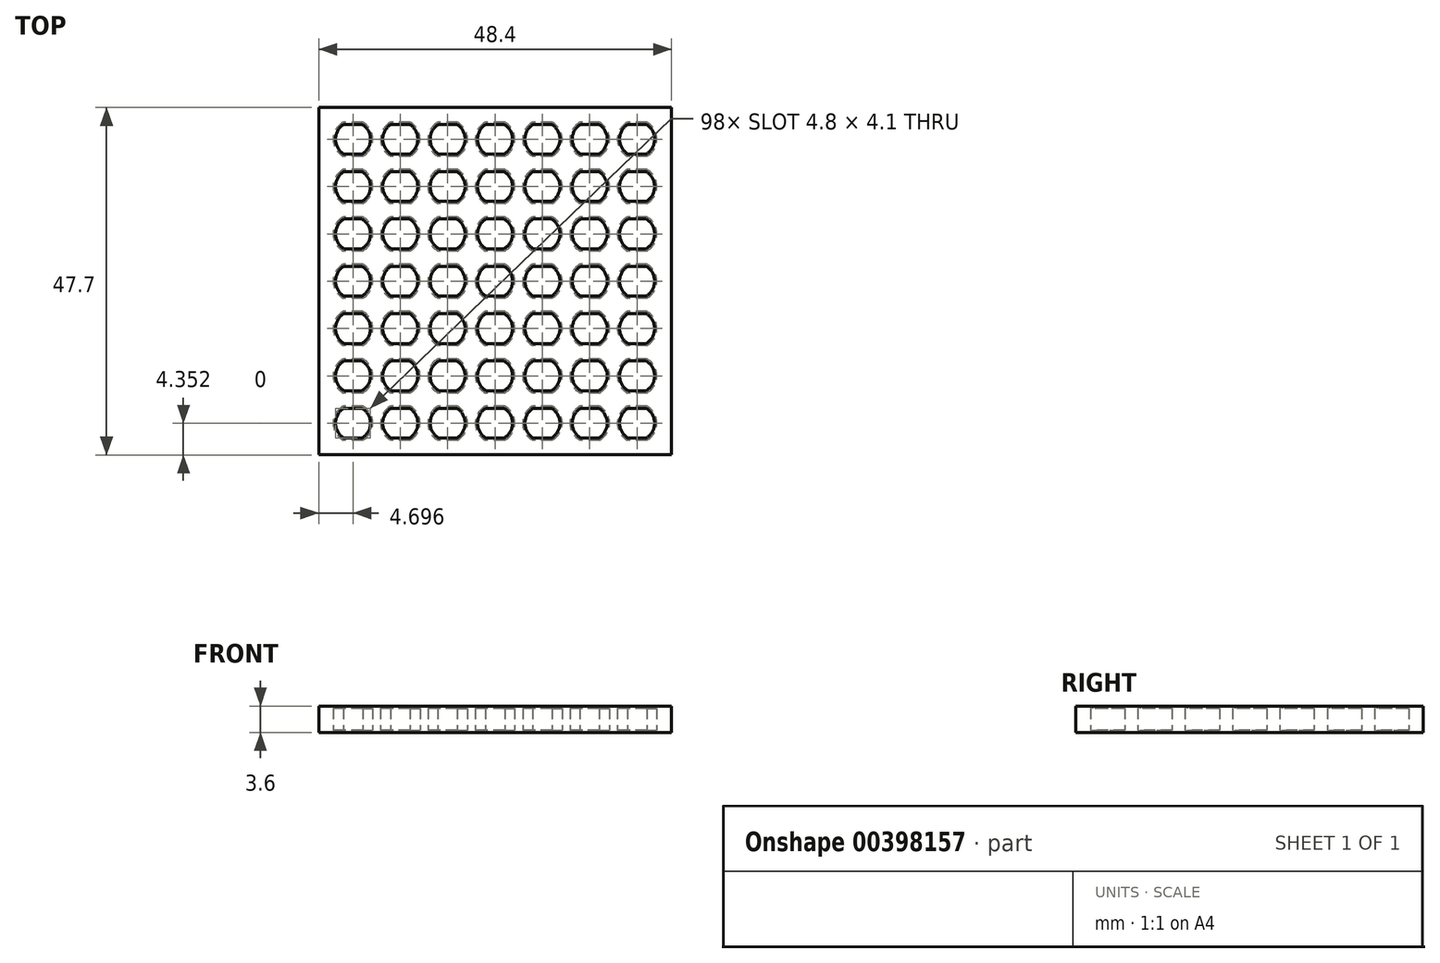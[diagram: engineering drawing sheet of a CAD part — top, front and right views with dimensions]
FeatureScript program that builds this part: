
annotation { "Feature Type Name" : "Feature", "Feature Type Description" : "" }
export const myFeature = defineFeature(function(context is Context, id is Id, definition is map)
    precondition{}
    {
        {
            var Q0;
            Q0=qCreatedBy(makeId("Top.planeOp"),FACE);
            var sketch = newSketch(context, id + "F0", { "sketchPlane" : qUnion([Q0])});
            skLineSegment(sketch, "E0.bottom", {"start": v(27.32, -19.22) * mm, "end": v(-27.32, -19.22) * mm, "construction": true});
            skLineSegment(sketch, "E0.top", {"start": v(27.32, 19.22) * mm, "end": v(-27.32, 19.22) * mm, "construction": true});
            skLineSegment(sketch, "E0.left", {"start": v(27.32, -19.22) * mm, "end": v(27.32, 19.22) * mm, "construction": true});
            skLineSegment(sketch, "E0.right", {"start": v(-27.32, -19.22) * mm, "end": v(-27.32, 19.22) * mm, "construction": true});
            skPoint(sketch, "E0.middle", {"position": v(0, 0) * mm});
            skArc(sketch, "E1", {"start": v(-23.3, 14.17) * mm, "mid": v(-21.92, 16.52) * mm, "end": v(-23.3, 18.87) * mm});
            skLineSegment(sketch, "E2.bottom", {"start": v(-23.3, 18.87) * mm, "end": v(-25.95, 18.87) * mm});
            skLineSegment(sketch, "E2.top", {"start": v(-23.3, 14.17) * mm, "end": v(-25.95, 14.17) * mm});
            skPoint(sketch, "E3.orphan", {"position": v(-21.92, 14.17) * mm});
            skPoint(sketch, "E4.orphan", {"position": v(-21.92, 18.87) * mm});
            skArc(sketch, "E5.trimOffspring", {"start": v(-25.95, 18.87) * mm, "mid": v(-27.32, 16.52) * mm, "end": v(-25.95, 14.17) * mm});
            skArc(sketch, "E6.0.1.0", {"start": v(-25.95, 12.37) * mm, "mid": v(-27.32, 10.02) * mm, "end": v(-25.95, 7.67) * mm});
            skLineSegment(sketch, "E6.0.1.1", {"start": v(-23.3, 7.67) * mm, "end": v(-25.95, 7.67) * mm});
            skLineSegment(sketch, "E6.0.1.2", {"start": v(-23.3, 12.37) * mm, "end": v(-25.95, 12.37) * mm});
            skArc(sketch, "E6.0.1.3", {"start": v(-23.3, 7.67) * mm, "mid": v(-21.92, 10.02) * mm, "end": v(-23.3, 12.37) * mm});
            skArc(sketch, "E6.0.2.0", {"start": v(-25.95, 5.87) * mm, "mid": v(-27.32, 3.52) * mm, "end": v(-25.95, 1.17) * mm});
            skLineSegment(sketch, "E6.0.2.1", {"start": v(-23.3, 1.17) * mm, "end": v(-25.95, 1.17) * mm});
            skLineSegment(sketch, "E6.0.2.2", {"start": v(-23.3, 5.87) * mm, "end": v(-25.95, 5.87) * mm});
            skArc(sketch, "E6.0.2.3", {"start": v(-23.3, 1.17) * mm, "mid": v(-21.92, 3.52) * mm, "end": v(-23.3, 5.87) * mm});
            skArc(sketch, "E6.1.0.0", {"start": v(-19.45, 18.87) * mm, "mid": v(-20.82, 16.52) * mm, "end": v(-19.45, 14.17) * mm});
            skLineSegment(sketch, "E6.1.0.1", {"start": v(-16.8, 14.17) * mm, "end": v(-19.45, 14.17) * mm});
            skLineSegment(sketch, "E6.1.0.2", {"start": v(-16.8, 18.87) * mm, "end": v(-19.45, 18.87) * mm});
            skArc(sketch, "E6.1.0.3", {"start": v(-16.8, 14.17) * mm, "mid": v(-15.42, 16.52) * mm, "end": v(-16.8, 18.87) * mm});
            skArc(sketch, "E6.1.1.0", {"start": v(-19.45, 12.37) * mm, "mid": v(-20.82, 10.02) * mm, "end": v(-19.45, 7.67) * mm});
            skLineSegment(sketch, "E6.1.1.1", {"start": v(-16.8, 7.67) * mm, "end": v(-19.45, 7.67) * mm});
            skLineSegment(sketch, "E6.1.1.2", {"start": v(-16.8, 12.37) * mm, "end": v(-19.45, 12.37) * mm});
            skArc(sketch, "E6.1.1.3", {"start": v(-16.8, 7.67) * mm, "mid": v(-15.42, 10.02) * mm, "end": v(-16.8, 12.37) * mm});
            skArc(sketch, "E6.1.2.0", {"start": v(-19.45, 5.87) * mm, "mid": v(-20.82, 3.52) * mm, "end": v(-19.45, 1.17) * mm});
            skLineSegment(sketch, "E6.1.2.1", {"start": v(-16.8, 1.17) * mm, "end": v(-19.45, 1.17) * mm});
            skLineSegment(sketch, "E6.1.2.2", {"start": v(-16.8, 5.87) * mm, "end": v(-19.45, 5.87) * mm});
            skArc(sketch, "E6.1.2.3", {"start": v(-16.8, 1.17) * mm, "mid": v(-15.42, 3.52) * mm, "end": v(-16.8, 5.87) * mm});
            skArc(sketch, "E6.2.0.0", {"start": v(-12.95, 18.87) * mm, "mid": v(-14.32, 16.52) * mm, "end": v(-12.95, 14.17) * mm});
            skLineSegment(sketch, "E6.2.0.1", {"start": v(-10.3, 14.17) * mm, "end": v(-12.95, 14.17) * mm});
            skLineSegment(sketch, "E6.2.0.2", {"start": v(-10.3, 18.87) * mm, "end": v(-12.95, 18.87) * mm});
            skArc(sketch, "E6.2.0.3", {"start": v(-10.3, 14.17) * mm, "mid": v(-8.92, 16.52) * mm, "end": v(-10.3, 18.87) * mm});
            skArc(sketch, "E6.2.1.0", {"start": v(-12.95, 12.37) * mm, "mid": v(-14.32, 10.02) * mm, "end": v(-12.95, 7.67) * mm});
            skLineSegment(sketch, "E6.2.1.1", {"start": v(-10.3, 7.67) * mm, "end": v(-12.95, 7.67) * mm});
            skLineSegment(sketch, "E6.2.1.2", {"start": v(-10.3, 12.37) * mm, "end": v(-12.95, 12.37) * mm});
            skArc(sketch, "E6.2.1.3", {"start": v(-10.3, 7.67) * mm, "mid": v(-8.92, 10.02) * mm, "end": v(-10.3, 12.37) * mm});
            skArc(sketch, "E6.2.2.0", {"start": v(-12.95, 5.87) * mm, "mid": v(-14.32, 3.52) * mm, "end": v(-12.95, 1.17) * mm});
            skLineSegment(sketch, "E6.2.2.1", {"start": v(-10.3, 1.17) * mm, "end": v(-12.95, 1.17) * mm});
            skLineSegment(sketch, "E6.2.2.2", {"start": v(-10.3, 5.87) * mm, "end": v(-12.95, 5.87) * mm});
            skArc(sketch, "E6.2.2.3", {"start": v(-10.3, 1.17) * mm, "mid": v(-8.92, 3.52) * mm, "end": v(-10.3, 5.87) * mm});
            skArc(sketch, "E6.3.0.0", {"start": v(-6.45, 18.87) * mm, "mid": v(-7.82, 16.52) * mm, "end": v(-6.45, 14.17) * mm});
            skLineSegment(sketch, "E6.3.0.1", {"start": v(-3.8, 14.17) * mm, "end": v(-6.45, 14.17) * mm});
            skLineSegment(sketch, "E6.3.0.2", {"start": v(-3.8, 18.87) * mm, "end": v(-6.45, 18.87) * mm});
            skArc(sketch, "E6.3.0.3", {"start": v(-3.8, 14.17) * mm, "mid": v(-2.42, 16.52) * mm, "end": v(-3.8, 18.87) * mm});
            skArc(sketch, "E6.3.1.0", {"start": v(-6.45, 12.37) * mm, "mid": v(-7.82, 10.02) * mm, "end": v(-6.45, 7.67) * mm});
            skLineSegment(sketch, "E6.3.1.1", {"start": v(-3.8, 7.67) * mm, "end": v(-6.45, 7.67) * mm});
            skLineSegment(sketch, "E6.3.1.2", {"start": v(-3.8, 12.37) * mm, "end": v(-6.45, 12.37) * mm});
            skArc(sketch, "E6.3.1.3", {"start": v(-3.8, 7.67) * mm, "mid": v(-2.42, 10.02) * mm, "end": v(-3.8, 12.37) * mm});
            skArc(sketch, "E6.3.2.0", {"start": v(-6.45, 5.87) * mm, "mid": v(-7.82, 3.52) * mm, "end": v(-6.45, 1.17) * mm});
            skLineSegment(sketch, "E6.3.2.1", {"start": v(-3.8, 1.17) * mm, "end": v(-6.45, 1.17) * mm});
            skLineSegment(sketch, "E6.3.2.2", {"start": v(-3.8, 5.87) * mm, "end": v(-6.45, 5.87) * mm});
            skArc(sketch, "E6.3.2.3", {"start": v(-3.8, 1.17) * mm, "mid": v(-2.42, 3.52) * mm, "end": v(-3.8, 5.87) * mm});
            skLineSegment(sketch, "E6.direction1", {"start": v(-25.95, 14.17) * mm, "end": v(-19.45, 14.17) * mm, "construction": true});
            skLineSegment(sketch, "E6.direction2", {"start": v(-25.95, 14.17) * mm, "end": v(-25.95, 7.67) * mm, "construction": true});
            skLineSegment(sketch, "E7.bottom", {"start": v(-29.32, 20.87) * mm, "end": v(19.08, 20.87) * mm});
            skLineSegment(sketch, "E7.top", {"start": v(-29.32, -26.83) * mm, "end": v(19.08, -26.83) * mm});
            skLineSegment(sketch, "E7.left", {"start": v(-29.32, 20.87) * mm, "end": v(-29.32, -26.83) * mm});
            skLineSegment(sketch, "E7.right", {"start": v(19.08, 20.87) * mm, "end": v(19.08, -26.83) * mm});
            skArc(sketch, "E8.0.4.0", {"start": v(0.05, 18.87) * mm, "mid": v(-1.32, 16.52) * mm, "end": v(0.05, 14.17) * mm});
            skLineSegment(sketch, "E8.4.4.0", {"start": v(2.7, 14.17) * mm, "end": v(0.05, 14.17) * mm});
            skLineSegment(sketch, "E8.7.4.0", {"start": v(2.7, 18.87) * mm, "end": v(0.05, 18.87) * mm});
            skArc(sketch, "E8.10.4.0", {"start": v(2.7, 14.17) * mm, "mid": v(4.08, 16.52) * mm, "end": v(2.7, 18.87) * mm});
            skArc(sketch, "E8.0.4.1", {"start": v(0.05, 12.37) * mm, "mid": v(-1.32, 10.02) * mm, "end": v(0.05, 7.67) * mm});
            skLineSegment(sketch, "E8.4.4.1", {"start": v(2.7, 7.67) * mm, "end": v(0.05, 7.67) * mm});
            skLineSegment(sketch, "E8.7.4.1", {"start": v(2.7, 12.37) * mm, "end": v(0.05, 12.37) * mm});
            skArc(sketch, "E8.10.4.1", {"start": v(2.7, 7.67) * mm, "mid": v(4.08, 10.02) * mm, "end": v(2.7, 12.37) * mm});
            skArc(sketch, "E8.0.4.2", {"start": v(0.05, 5.87) * mm, "mid": v(-1.32, 3.52) * mm, "end": v(0.05, 1.17) * mm});
            skLineSegment(sketch, "E8.4.4.2", {"start": v(2.7, 1.17) * mm, "end": v(0.05, 1.17) * mm});
            skLineSegment(sketch, "E8.7.4.2", {"start": v(2.7, 5.87) * mm, "end": v(0.05, 5.87) * mm});
            skArc(sketch, "E8.10.4.2", {"start": v(2.7, 1.17) * mm, "mid": v(4.08, 3.52) * mm, "end": v(2.7, 5.87) * mm});
            skArc(sketch, "E8.0.5.0", {"start": v(6.55, 18.87) * mm, "mid": v(5.18, 16.52) * mm, "end": v(6.55, 14.17) * mm});
            skLineSegment(sketch, "E8.4.5.0", {"start": v(9.2, 14.17) * mm, "end": v(6.55, 14.17) * mm});
            skLineSegment(sketch, "E8.7.5.0", {"start": v(9.2, 18.87) * mm, "end": v(6.55, 18.87) * mm});
            skArc(sketch, "E8.10.5.0", {"start": v(9.2, 14.17) * mm, "mid": v(10.58, 16.52) * mm, "end": v(9.2, 18.87) * mm});
            skArc(sketch, "E8.0.5.1", {"start": v(6.55, 12.37) * mm, "mid": v(5.18, 10.02) * mm, "end": v(6.55, 7.67) * mm});
            skLineSegment(sketch, "E8.4.5.1", {"start": v(9.2, 7.67) * mm, "end": v(6.55, 7.67) * mm});
            skLineSegment(sketch, "E8.7.5.1", {"start": v(9.2, 12.37) * mm, "end": v(6.55, 12.37) * mm});
            skArc(sketch, "E8.10.5.1", {"start": v(9.2, 7.67) * mm, "mid": v(10.58, 10.02) * mm, "end": v(9.2, 12.37) * mm});
            skArc(sketch, "E8.0.5.2", {"start": v(6.55, 5.87) * mm, "mid": v(5.18, 3.52) * mm, "end": v(6.55, 1.17) * mm});
            skLineSegment(sketch, "E8.4.5.2", {"start": v(9.2, 1.17) * mm, "end": v(6.55, 1.17) * mm});
            skLineSegment(sketch, "E8.7.5.2", {"start": v(9.2, 5.87) * mm, "end": v(6.55, 5.87) * mm});
            skArc(sketch, "E8.10.5.2", {"start": v(9.2, 1.17) * mm, "mid": v(10.58, 3.52) * mm, "end": v(9.2, 5.87) * mm});
            skArc(sketch, "E8.0.6.0", {"start": v(13.05, 18.87) * mm, "mid": v(11.68, 16.52) * mm, "end": v(13.05, 14.17) * mm});
            skLineSegment(sketch, "E8.4.6.0", {"start": v(15.7, 14.17) * mm, "end": v(13.05, 14.17) * mm});
            skLineSegment(sketch, "E8.7.6.0", {"start": v(15.7, 18.87) * mm, "end": v(13.05, 18.87) * mm});
            skArc(sketch, "E8.10.6.0", {"start": v(15.7, 14.17) * mm, "mid": v(17.08, 16.52) * mm, "end": v(15.7, 18.87) * mm});
            skArc(sketch, "E8.0.6.1", {"start": v(13.05, 12.37) * mm, "mid": v(11.68, 10.02) * mm, "end": v(13.05, 7.67) * mm});
            skLineSegment(sketch, "E8.4.6.1", {"start": v(15.7, 7.67) * mm, "end": v(13.05, 7.67) * mm});
            skLineSegment(sketch, "E8.7.6.1", {"start": v(15.7, 12.37) * mm, "end": v(13.05, 12.37) * mm});
            skArc(sketch, "E8.10.6.1", {"start": v(15.7, 7.67) * mm, "mid": v(17.08, 10.02) * mm, "end": v(15.7, 12.37) * mm});
            skArc(sketch, "E8.0.6.2", {"start": v(13.05, 5.87) * mm, "mid": v(11.68, 3.52) * mm, "end": v(13.05, 1.17) * mm});
            skLineSegment(sketch, "E8.4.6.2", {"start": v(15.7, 1.17) * mm, "end": v(13.05, 1.17) * mm});
            skLineSegment(sketch, "E8.7.6.2", {"start": v(15.7, 5.87) * mm, "end": v(13.05, 5.87) * mm});
            skArc(sketch, "E8.10.6.2", {"start": v(15.7, 1.17) * mm, "mid": v(17.08, 3.52) * mm, "end": v(15.7, 5.87) * mm});
            skArc(sketch, "E9.0.0.3", {"start": v(-25.95, -0.63) * mm, "mid": v(-27.32, -2.98) * mm, "end": v(-25.95, -5.33) * mm});
            skLineSegment(sketch, "E9.4.0.3", {"start": v(-23.3, -5.33) * mm, "end": v(-25.95, -5.33) * mm});
            skLineSegment(sketch, "E9.7.0.3", {"start": v(-23.3, -0.63) * mm, "end": v(-25.95, -0.63) * mm});
            skArc(sketch, "E9.10.0.3", {"start": v(-23.3, -5.33) * mm, "mid": v(-21.92, -2.98) * mm, "end": v(-23.3, -0.63) * mm});
            skArc(sketch, "E9.0.0.4", {"start": v(-25.95, -7.13) * mm, "mid": v(-27.32, -9.48) * mm, "end": v(-25.95, -11.83) * mm});
            skLineSegment(sketch, "E9.4.0.4", {"start": v(-23.3, -11.83) * mm, "end": v(-25.95, -11.83) * mm});
            skLineSegment(sketch, "E9.7.0.4", {"start": v(-23.3, -7.13) * mm, "end": v(-25.95, -7.13) * mm});
            skArc(sketch, "E9.10.0.4", {"start": v(-23.3, -11.83) * mm, "mid": v(-21.92, -9.48) * mm, "end": v(-23.3, -7.13) * mm});
            skArc(sketch, "E9.0.0.5", {"start": v(-25.95, -13.63) * mm, "mid": v(-27.32, -15.98) * mm, "end": v(-25.95, -18.33) * mm});
            skLineSegment(sketch, "E9.4.0.5", {"start": v(-23.3, -18.33) * mm, "end": v(-25.95, -18.33) * mm});
            skLineSegment(sketch, "E9.7.0.5", {"start": v(-23.3, -13.63) * mm, "end": v(-25.95, -13.63) * mm});
            skArc(sketch, "E9.10.0.5", {"start": v(-23.3, -18.33) * mm, "mid": v(-21.92, -15.98) * mm, "end": v(-23.3, -13.63) * mm});
            skArc(sketch, "E9.0.0.6", {"start": v(-25.95, -20.13) * mm, "mid": v(-27.32, -22.48) * mm, "end": v(-25.95, -24.83) * mm});
            skLineSegment(sketch, "E9.4.0.6", {"start": v(-23.3, -24.83) * mm, "end": v(-25.95, -24.83) * mm});
            skLineSegment(sketch, "E9.7.0.6", {"start": v(-23.3, -20.13) * mm, "end": v(-25.95, -20.13) * mm});
            skArc(sketch, "E9.10.0.6", {"start": v(-23.3, -24.83) * mm, "mid": v(-21.92, -22.48) * mm, "end": v(-23.3, -20.13) * mm});
            skArc(sketch, "E9.0.1.3", {"start": v(-19.45, -0.63) * mm, "mid": v(-20.82, -2.98) * mm, "end": v(-19.45, -5.33) * mm});
            skLineSegment(sketch, "E9.4.1.3", {"start": v(-16.8, -5.33) * mm, "end": v(-19.45, -5.33) * mm});
            skLineSegment(sketch, "E9.7.1.3", {"start": v(-16.8, -0.63) * mm, "end": v(-19.45, -0.63) * mm});
            skArc(sketch, "E9.10.1.3", {"start": v(-16.8, -5.33) * mm, "mid": v(-15.42, -2.98) * mm, "end": v(-16.8, -0.63) * mm});
            skArc(sketch, "E9.0.1.4", {"start": v(-19.45, -7.13) * mm, "mid": v(-20.82, -9.48) * mm, "end": v(-19.45, -11.83) * mm});
            skLineSegment(sketch, "E9.4.1.4", {"start": v(-16.8, -11.83) * mm, "end": v(-19.45, -11.83) * mm});
            skLineSegment(sketch, "E9.7.1.4", {"start": v(-16.8, -7.13) * mm, "end": v(-19.45, -7.13) * mm});
            skArc(sketch, "E9.10.1.4", {"start": v(-16.8, -11.83) * mm, "mid": v(-15.42, -9.48) * mm, "end": v(-16.8, -7.13) * mm});
            skArc(sketch, "E9.0.1.5", {"start": v(-19.45, -13.63) * mm, "mid": v(-20.82, -15.98) * mm, "end": v(-19.45, -18.33) * mm});
            skLineSegment(sketch, "E9.4.1.5", {"start": v(-16.8, -18.33) * mm, "end": v(-19.45, -18.33) * mm});
            skLineSegment(sketch, "E9.7.1.5", {"start": v(-16.8, -13.63) * mm, "end": v(-19.45, -13.63) * mm});
            skArc(sketch, "E9.10.1.5", {"start": v(-16.8, -18.33) * mm, "mid": v(-15.42, -15.98) * mm, "end": v(-16.8, -13.63) * mm});
            skArc(sketch, "E9.0.1.6", {"start": v(-19.45, -20.13) * mm, "mid": v(-20.82, -22.48) * mm, "end": v(-19.45, -24.83) * mm});
            skLineSegment(sketch, "E9.4.1.6", {"start": v(-16.8, -24.83) * mm, "end": v(-19.45, -24.83) * mm});
            skLineSegment(sketch, "E9.7.1.6", {"start": v(-16.8, -20.13) * mm, "end": v(-19.45, -20.13) * mm});
            skArc(sketch, "E9.10.1.6", {"start": v(-16.8, -24.83) * mm, "mid": v(-15.42, -22.48) * mm, "end": v(-16.8, -20.13) * mm});
            skArc(sketch, "E9.0.2.3", {"start": v(-12.95, -0.63) * mm, "mid": v(-14.32, -2.98) * mm, "end": v(-12.95, -5.33) * mm});
            skLineSegment(sketch, "E9.4.2.3", {"start": v(-10.3, -5.33) * mm, "end": v(-12.95, -5.33) * mm});
            skLineSegment(sketch, "E9.7.2.3", {"start": v(-10.3, -0.63) * mm, "end": v(-12.95, -0.63) * mm});
            skArc(sketch, "E9.10.2.3", {"start": v(-10.3, -5.33) * mm, "mid": v(-8.92, -2.98) * mm, "end": v(-10.3, -0.63) * mm});
            skArc(sketch, "E9.0.2.4", {"start": v(-12.95, -7.13) * mm, "mid": v(-14.32, -9.48) * mm, "end": v(-12.95, -11.83) * mm});
            skLineSegment(sketch, "E9.4.2.4", {"start": v(-10.3, -11.83) * mm, "end": v(-12.95, -11.83) * mm});
            skLineSegment(sketch, "E9.7.2.4", {"start": v(-10.3, -7.13) * mm, "end": v(-12.95, -7.13) * mm});
            skArc(sketch, "E9.10.2.4", {"start": v(-10.3, -11.83) * mm, "mid": v(-8.92, -9.48) * mm, "end": v(-10.3, -7.13) * mm});
            skArc(sketch, "E9.0.2.5", {"start": v(-12.95, -13.63) * mm, "mid": v(-14.32, -15.98) * mm, "end": v(-12.95, -18.33) * mm});
            skLineSegment(sketch, "E9.4.2.5", {"start": v(-10.3, -18.33) * mm, "end": v(-12.95, -18.33) * mm});
            skLineSegment(sketch, "E9.7.2.5", {"start": v(-10.3, -13.63) * mm, "end": v(-12.95, -13.63) * mm});
            skArc(sketch, "E9.10.2.5", {"start": v(-10.3, -18.33) * mm, "mid": v(-8.92, -15.98) * mm, "end": v(-10.3, -13.63) * mm});
            skArc(sketch, "E9.0.2.6", {"start": v(-12.95, -20.13) * mm, "mid": v(-14.32, -22.48) * mm, "end": v(-12.95, -24.83) * mm});
            skLineSegment(sketch, "E9.4.2.6", {"start": v(-10.3, -24.83) * mm, "end": v(-12.95, -24.83) * mm});
            skLineSegment(sketch, "E9.7.2.6", {"start": v(-10.3, -20.13) * mm, "end": v(-12.95, -20.13) * mm});
            skArc(sketch, "E9.10.2.6", {"start": v(-10.3, -24.83) * mm, "mid": v(-8.92, -22.48) * mm, "end": v(-10.3, -20.13) * mm});
            skArc(sketch, "E9.0.3.3", {"start": v(-6.45, -0.63) * mm, "mid": v(-7.82, -2.98) * mm, "end": v(-6.45, -5.33) * mm});
            skLineSegment(sketch, "E9.4.3.3", {"start": v(-3.8, -5.33) * mm, "end": v(-6.45, -5.33) * mm});
            skLineSegment(sketch, "E9.7.3.3", {"start": v(-3.8, -0.63) * mm, "end": v(-6.45, -0.63) * mm});
            skArc(sketch, "E9.10.3.3", {"start": v(-3.8, -5.33) * mm, "mid": v(-2.42, -2.98) * mm, "end": v(-3.8, -0.63) * mm});
            skArc(sketch, "E9.0.3.4", {"start": v(-6.45, -7.13) * mm, "mid": v(-7.82, -9.48) * mm, "end": v(-6.45, -11.83) * mm});
            skLineSegment(sketch, "E9.4.3.4", {"start": v(-3.8, -11.83) * mm, "end": v(-6.45, -11.83) * mm});
            skLineSegment(sketch, "E9.7.3.4", {"start": v(-3.8, -7.13) * mm, "end": v(-6.45, -7.13) * mm});
            skArc(sketch, "E9.10.3.4", {"start": v(-3.8, -11.83) * mm, "mid": v(-2.42, -9.48) * mm, "end": v(-3.8, -7.13) * mm});
            skArc(sketch, "E9.0.3.5", {"start": v(-6.45, -13.63) * mm, "mid": v(-7.82, -15.98) * mm, "end": v(-6.45, -18.33) * mm});
            skLineSegment(sketch, "E9.4.3.5", {"start": v(-3.8, -18.33) * mm, "end": v(-6.45, -18.33) * mm});
            skLineSegment(sketch, "E9.7.3.5", {"start": v(-3.8, -13.63) * mm, "end": v(-6.45, -13.63) * mm});
            skArc(sketch, "E9.10.3.5", {"start": v(-3.8, -18.33) * mm, "mid": v(-2.42, -15.98) * mm, "end": v(-3.8, -13.63) * mm});
            skArc(sketch, "E9.0.3.6", {"start": v(-6.45, -20.13) * mm, "mid": v(-7.82, -22.48) * mm, "end": v(-6.45, -24.83) * mm});
            skLineSegment(sketch, "E9.4.3.6", {"start": v(-3.8, -24.83) * mm, "end": v(-6.45, -24.83) * mm});
            skLineSegment(sketch, "E9.7.3.6", {"start": v(-3.8, -20.13) * mm, "end": v(-6.45, -20.13) * mm});
            skArc(sketch, "E9.10.3.6", {"start": v(-3.8, -24.83) * mm, "mid": v(-2.42, -22.48) * mm, "end": v(-3.8, -20.13) * mm});
            skArc(sketch, "E9.0.4.3", {"start": v(0.05, -0.63) * mm, "mid": v(-1.32, -2.98) * mm, "end": v(0.05, -5.33) * mm});
            skLineSegment(sketch, "E9.4.4.3", {"start": v(2.7, -5.33) * mm, "end": v(0.05, -5.33) * mm});
            skLineSegment(sketch, "E9.7.4.3", {"start": v(2.7, -0.63) * mm, "end": v(0.05, -0.63) * mm});
            skArc(sketch, "E9.10.4.3", {"start": v(2.7, -5.33) * mm, "mid": v(4.08, -2.98) * mm, "end": v(2.7, -0.63) * mm});
            skArc(sketch, "E9.0.4.4", {"start": v(0.05, -7.13) * mm, "mid": v(-1.32, -9.48) * mm, "end": v(0.05, -11.83) * mm});
            skLineSegment(sketch, "E9.4.4.4", {"start": v(2.7, -11.83) * mm, "end": v(0.05, -11.83) * mm});
            skLineSegment(sketch, "E9.7.4.4", {"start": v(2.7, -7.13) * mm, "end": v(0.05, -7.13) * mm});
            skArc(sketch, "E9.10.4.4", {"start": v(2.7, -11.83) * mm, "mid": v(4.08, -9.48) * mm, "end": v(2.7, -7.13) * mm});
            skArc(sketch, "E9.0.4.5", {"start": v(0.05, -13.63) * mm, "mid": v(-1.32, -15.98) * mm, "end": v(0.05, -18.33) * mm});
            skLineSegment(sketch, "E9.4.4.5", {"start": v(2.7, -18.33) * mm, "end": v(0.05, -18.33) * mm});
            skLineSegment(sketch, "E9.7.4.5", {"start": v(2.7, -13.63) * mm, "end": v(0.05, -13.63) * mm});
            skArc(sketch, "E9.10.4.5", {"start": v(2.7, -18.33) * mm, "mid": v(4.08, -15.98) * mm, "end": v(2.7, -13.63) * mm});
            skArc(sketch, "E9.0.4.6", {"start": v(0.05, -20.13) * mm, "mid": v(-1.32, -22.48) * mm, "end": v(0.05, -24.83) * mm});
            skLineSegment(sketch, "E9.4.4.6", {"start": v(2.7, -24.83) * mm, "end": v(0.05, -24.83) * mm});
            skLineSegment(sketch, "E9.7.4.6", {"start": v(2.7, -20.13) * mm, "end": v(0.05, -20.13) * mm});
            skArc(sketch, "E9.10.4.6", {"start": v(2.7, -24.83) * mm, "mid": v(4.08, -22.48) * mm, "end": v(2.7, -20.13) * mm});
            skArc(sketch, "E9.0.5.3", {"start": v(6.55, -0.63) * mm, "mid": v(5.18, -2.98) * mm, "end": v(6.55, -5.33) * mm});
            skLineSegment(sketch, "E9.4.5.3", {"start": v(9.2, -5.33) * mm, "end": v(6.55, -5.33) * mm});
            skLineSegment(sketch, "E9.7.5.3", {"start": v(9.2, -0.63) * mm, "end": v(6.55, -0.63) * mm});
            skArc(sketch, "E9.10.5.3", {"start": v(9.2, -5.33) * mm, "mid": v(10.58, -2.98) * mm, "end": v(9.2, -0.63) * mm});
            skArc(sketch, "E9.0.5.4", {"start": v(6.55, -7.13) * mm, "mid": v(5.18, -9.48) * mm, "end": v(6.55, -11.83) * mm});
            skLineSegment(sketch, "E9.4.5.4", {"start": v(9.2, -11.83) * mm, "end": v(6.55, -11.83) * mm});
            skLineSegment(sketch, "E9.7.5.4", {"start": v(9.2, -7.13) * mm, "end": v(6.55, -7.13) * mm});
            skArc(sketch, "E9.10.5.4", {"start": v(9.2, -11.83) * mm, "mid": v(10.58, -9.48) * mm, "end": v(9.2, -7.13) * mm});
            skArc(sketch, "E9.0.5.5", {"start": v(6.55, -13.63) * mm, "mid": v(5.18, -15.98) * mm, "end": v(6.55, -18.33) * mm});
            skLineSegment(sketch, "E9.4.5.5", {"start": v(9.2, -18.33) * mm, "end": v(6.55, -18.33) * mm});
            skLineSegment(sketch, "E9.7.5.5", {"start": v(9.2, -13.63) * mm, "end": v(6.55, -13.63) * mm});
            skArc(sketch, "E9.10.5.5", {"start": v(9.2, -18.33) * mm, "mid": v(10.58, -15.98) * mm, "end": v(9.2, -13.63) * mm});
            skArc(sketch, "E9.0.5.6", {"start": v(6.55, -20.13) * mm, "mid": v(5.18, -22.48) * mm, "end": v(6.55, -24.83) * mm});
            skLineSegment(sketch, "E9.4.5.6", {"start": v(9.2, -24.83) * mm, "end": v(6.55, -24.83) * mm});
            skLineSegment(sketch, "E9.7.5.6", {"start": v(9.2, -20.13) * mm, "end": v(6.55, -20.13) * mm});
            skArc(sketch, "E9.10.5.6", {"start": v(9.2, -24.83) * mm, "mid": v(10.58, -22.48) * mm, "end": v(9.2, -20.13) * mm});
            skArc(sketch, "E9.0.6.3", {"start": v(13.05, -0.63) * mm, "mid": v(11.68, -2.98) * mm, "end": v(13.05, -5.33) * mm});
            skLineSegment(sketch, "E9.4.6.3", {"start": v(15.7, -5.33) * mm, "end": v(13.05, -5.33) * mm});
            skLineSegment(sketch, "E9.7.6.3", {"start": v(15.7, -0.63) * mm, "end": v(13.05, -0.63) * mm});
            skArc(sketch, "E9.10.6.3", {"start": v(15.7, -5.33) * mm, "mid": v(17.08, -2.98) * mm, "end": v(15.7, -0.63) * mm});
            skArc(sketch, "E9.0.6.4", {"start": v(13.05, -7.13) * mm, "mid": v(11.68, -9.48) * mm, "end": v(13.05, -11.83) * mm});
            skLineSegment(sketch, "E9.4.6.4", {"start": v(15.7, -11.83) * mm, "end": v(13.05, -11.83) * mm});
            skLineSegment(sketch, "E9.7.6.4", {"start": v(15.7, -7.13) * mm, "end": v(13.05, -7.13) * mm});
            skArc(sketch, "E9.10.6.4", {"start": v(15.7, -11.83) * mm, "mid": v(17.08, -9.48) * mm, "end": v(15.7, -7.13) * mm});
            skArc(sketch, "E9.0.6.5", {"start": v(13.05, -13.63) * mm, "mid": v(11.68, -15.98) * mm, "end": v(13.05, -18.33) * mm});
            skLineSegment(sketch, "E9.4.6.5", {"start": v(15.7, -18.33) * mm, "end": v(13.05, -18.33) * mm});
            skLineSegment(sketch, "E9.7.6.5", {"start": v(15.7, -13.63) * mm, "end": v(13.05, -13.63) * mm});
            skArc(sketch, "E9.10.6.5", {"start": v(15.7, -18.33) * mm, "mid": v(17.08, -15.98) * mm, "end": v(15.7, -13.63) * mm});
            skArc(sketch, "E9.0.6.6", {"start": v(13.05, -20.13) * mm, "mid": v(11.68, -22.48) * mm, "end": v(13.05, -24.83) * mm});
            skLineSegment(sketch, "E9.4.6.6", {"start": v(15.7, -24.83) * mm, "end": v(13.05, -24.83) * mm});
            skLineSegment(sketch, "E9.7.6.6", {"start": v(15.7, -20.13) * mm, "end": v(13.05, -20.13) * mm});
            skArc(sketch, "E9.10.6.6", {"start": v(15.7, -24.83) * mm, "mid": v(17.08, -22.48) * mm, "end": v(15.7, -20.13) * mm});
            skLineSegment(sketch, "E10.bottom", {"start": v(-24.62, 16.52) * mm, "end": v(-18.12, 16.52) * mm, "construction": true});
            skLineSegment(sketch, "E10.top", {"start": v(-24.62, 10.02) * mm, "end": v(-18.12, 10.02) * mm, "construction": true});
            skLineSegment(sketch, "E10.left", {"start": v(-24.62, 16.52) * mm, "end": v(-24.62, 10.02) * mm, "construction": true});
            skLineSegment(sketch, "E10.right", {"start": v(-18.12, 16.52) * mm, "end": v(-18.12, 10.02) * mm, "construction": true});
            skSolve(sketch);
        }
        {
            var Q0;
            Q0=qSketchRegion(id+"F0",true);
            extrude(context, id + "F1", {"entities" : qUnion([Q0]), "depth" : 3 * mm});
        }
        {
            var Q0;
            Q0=makeQuery(id+"F1.opExtrude","CAP_FACE",FACE,{"disambiguationData":[OSD([sQuery(id+"F0.wireOp",EDGE,"E1"),sQuery(id+"F0.wireOp",EDGE,"E2.bottom"),sQuery(id+"F0.wireOp",EDGE,"E2.top"),sQuery(id+"F0.wireOp",EDGE,"E5.trimOffspring"),sQuery(id+"F0.wireOp",EDGE,"E6.0.1.0"),sQuery(id+"F0.wireOp",EDGE,"E6.0.1.1"),sQuery(id+"F0.wireOp",EDGE,"E6.0.1.2"),sQuery(id+"F0.wireOp",EDGE,"E6.0.1.3"),sQuery(id+"F0.wireOp",EDGE,"E6.0.2.0"),sQuery(id+"F0.wireOp",EDGE,"E6.0.2.1"),sQuery(id+"F0.wireOp",EDGE,"E6.0.2.2"),sQuery(id+"F0.wireOp",EDGE,"E6.0.2.3"),sQuery(id+"F0.wireOp",EDGE,"E6.1.0.0"),sQuery(id+"F0.wireOp",EDGE,"E6.1.0.1"),sQuery(id+"F0.wireOp",EDGE,"E6.1.0.2"),sQuery(id+"F0.wireOp",EDGE,"E6.1.0.3"),sQuery(id+"F0.wireOp",EDGE,"E6.1.1.0"),sQuery(id+"F0.wireOp",EDGE,"E6.1.1.1"),sQuery(id+"F0.wireOp",EDGE,"E6.1.1.2"),sQuery(id+"F0.wireOp",EDGE,"E6.1.1.3"),sQuery(id+"F0.wireOp",EDGE,"E6.1.2.0"),sQuery(id+"F0.wireOp",EDGE,"E6.1.2.1"),sQuery(id+"F0.wireOp",EDGE,"E6.1.2.2"),sQuery(id+"F0.wireOp",EDGE,"E6.1.2.3"),sQuery(id+"F0.wireOp",EDGE,"E6.2.0.0"),sQuery(id+"F0.wireOp",EDGE,"E6.2.0.1"),sQuery(id+"F0.wireOp",EDGE,"E6.2.0.2"),sQuery(id+"F0.wireOp",EDGE,"E6.2.0.3"),sQuery(id+"F0.wireOp",EDGE,"E6.2.1.0"),sQuery(id+"F0.wireOp",EDGE,"E6.2.1.1"),sQuery(id+"F0.wireOp",EDGE,"E6.2.1.2"),sQuery(id+"F0.wireOp",EDGE,"E6.2.1.3"),sQuery(id+"F0.wireOp",EDGE,"E6.2.2.0"),sQuery(id+"F0.wireOp",EDGE,"E6.2.2.1"),sQuery(id+"F0.wireOp",EDGE,"E6.2.2.2"),sQuery(id+"F0.wireOp",EDGE,"E6.2.2.3"),sQuery(id+"F0.wireOp",EDGE,"E6.3.0.0"),sQuery(id+"F0.wireOp",EDGE,"E6.3.0.1"),sQuery(id+"F0.wireOp",EDGE,"E6.3.0.2"),sQuery(id+"F0.wireOp",EDGE,"E6.3.0.3"),sQuery(id+"F0.wireOp",EDGE,"E6.3.1.0"),sQuery(id+"F0.wireOp",EDGE,"E6.3.1.1"),sQuery(id+"F0.wireOp",EDGE,"E6.3.1.2"),sQuery(id+"F0.wireOp",EDGE,"E6.3.1.3"),sQuery(id+"F0.wireOp",EDGE,"E6.3.2.0"),sQuery(id+"F0.wireOp",EDGE,"E6.3.2.1"),sQuery(id+"F0.wireOp",EDGE,"E6.3.2.2"),sQuery(id+"F0.wireOp",EDGE,"E6.3.2.3"),sQuery(id+"F0.wireOp",EDGE,"E7.bottom"),sQuery(id+"F0.wireOp",EDGE,"E7.top"),sQuery(id+"F0.wireOp",EDGE,"E7.left"),sQuery(id+"F0.wireOp",EDGE,"E7.right")])],"isStart":false});
            var sketch = newSketch(context, id + "F2", { "sketchPlane" : qUnion([Q0])});
            skLineSegment(sketch, "E11.0", {"start": v(-23.38, 18.57) * mm, "end": v(-25.87, 18.57) * mm});
            skArc(sketch, "E11.1", {"start": v(-23.38, 14.47) * mm, "mid": v(-22.22, 16.52) * mm, "end": v(-23.38, 18.57) * mm});
            skLineSegment(sketch, "E11.2", {"start": v(-23.38, 14.47) * mm, "end": v(-25.87, 14.47) * mm});
            skArc(sketch, "E11.3", {"start": v(-25.87, 18.57) * mm, "mid": v(-27.02, 16.52) * mm, "end": v(-25.87, 14.47) * mm});
            skArc(sketch, "E12.0.1.0", {"start": v(-25.87, 12.07) * mm, "mid": v(-27.02, 10.02) * mm, "end": v(-25.87, 7.97) * mm});
            skLineSegment(sketch, "E12.0.1.1", {"start": v(-23.38, 12.07) * mm, "end": v(-25.87, 12.07) * mm});
            skArc(sketch, "E12.0.1.2", {"start": v(-23.38, 7.97) * mm, "mid": v(-22.22, 10.02) * mm, "end": v(-23.38, 12.07) * mm});
            skLineSegment(sketch, "E12.0.1.3", {"start": v(-23.38, 7.97) * mm, "end": v(-25.87, 7.97) * mm});
            skArc(sketch, "E12.0.2.0", {"start": v(-25.87, 5.57) * mm, "mid": v(-27.02, 3.52) * mm, "end": v(-25.87, 1.47) * mm});
            skLineSegment(sketch, "E12.0.2.1", {"start": v(-23.38, 5.57) * mm, "end": v(-25.87, 5.57) * mm});
            skArc(sketch, "E12.0.2.2", {"start": v(-23.38, 1.47) * mm, "mid": v(-22.22, 3.52) * mm, "end": v(-23.38, 5.57) * mm});
            skLineSegment(sketch, "E12.0.2.3", {"start": v(-23.38, 1.47) * mm, "end": v(-25.87, 1.47) * mm});
            skArc(sketch, "E12.1.0.0", {"start": v(-19.37, 18.57) * mm, "mid": v(-20.52, 16.52) * mm, "end": v(-19.37, 14.47) * mm});
            skLineSegment(sketch, "E12.1.0.1", {"start": v(-16.88, 18.57) * mm, "end": v(-19.37, 18.57) * mm});
            skArc(sketch, "E12.1.0.2", {"start": v(-16.88, 14.47) * mm, "mid": v(-15.72, 16.52) * mm, "end": v(-16.88, 18.57) * mm});
            skLineSegment(sketch, "E12.1.0.3", {"start": v(-16.88, 14.47) * mm, "end": v(-19.37, 14.47) * mm});
            skArc(sketch, "E12.1.1.0", {"start": v(-19.37, 12.07) * mm, "mid": v(-20.52, 10.02) * mm, "end": v(-19.37, 7.97) * mm});
            skLineSegment(sketch, "E12.1.1.1", {"start": v(-16.88, 12.07) * mm, "end": v(-19.37, 12.07) * mm});
            skArc(sketch, "E12.1.1.2", {"start": v(-16.88, 7.97) * mm, "mid": v(-15.72, 10.02) * mm, "end": v(-16.88, 12.07) * mm});
            skLineSegment(sketch, "E12.1.1.3", {"start": v(-16.88, 7.97) * mm, "end": v(-19.37, 7.97) * mm});
            skArc(sketch, "E12.1.2.0", {"start": v(-19.37, 5.57) * mm, "mid": v(-20.52, 3.52) * mm, "end": v(-19.37, 1.47) * mm});
            skLineSegment(sketch, "E12.1.2.1", {"start": v(-16.88, 5.57) * mm, "end": v(-19.37, 5.57) * mm});
            skArc(sketch, "E12.1.2.2", {"start": v(-16.88, 1.47) * mm, "mid": v(-15.72, 3.52) * mm, "end": v(-16.88, 5.57) * mm});
            skLineSegment(sketch, "E12.1.2.3", {"start": v(-16.88, 1.47) * mm, "end": v(-19.37, 1.47) * mm});
            skArc(sketch, "E12.2.0.0", {"start": v(-12.87, 18.57) * mm, "mid": v(-14.02, 16.52) * mm, "end": v(-12.87, 14.47) * mm});
            skLineSegment(sketch, "E12.2.0.1", {"start": v(-10.38, 18.57) * mm, "end": v(-12.87, 18.57) * mm});
            skArc(sketch, "E12.2.0.2", {"start": v(-10.38, 14.47) * mm, "mid": v(-9.22, 16.52) * mm, "end": v(-10.38, 18.57) * mm});
            skLineSegment(sketch, "E12.2.0.3", {"start": v(-10.38, 14.47) * mm, "end": v(-12.87, 14.47) * mm});
            skArc(sketch, "E12.2.1.0", {"start": v(-12.87, 12.07) * mm, "mid": v(-14.02, 10.02) * mm, "end": v(-12.87, 7.97) * mm});
            skLineSegment(sketch, "E12.2.1.1", {"start": v(-10.38, 12.07) * mm, "end": v(-12.87, 12.07) * mm});
            skArc(sketch, "E12.2.1.2", {"start": v(-10.38, 7.97) * mm, "mid": v(-9.22, 10.02) * mm, "end": v(-10.38, 12.07) * mm});
            skLineSegment(sketch, "E12.2.1.3", {"start": v(-10.38, 7.97) * mm, "end": v(-12.87, 7.97) * mm});
            skArc(sketch, "E12.2.2.0", {"start": v(-12.87, 5.57) * mm, "mid": v(-14.02, 3.52) * mm, "end": v(-12.87, 1.47) * mm});
            skLineSegment(sketch, "E12.2.2.1", {"start": v(-10.38, 5.57) * mm, "end": v(-12.87, 5.57) * mm});
            skArc(sketch, "E12.2.2.2", {"start": v(-10.38, 1.47) * mm, "mid": v(-9.22, 3.52) * mm, "end": v(-10.38, 5.57) * mm});
            skLineSegment(sketch, "E12.2.2.3", {"start": v(-10.38, 1.47) * mm, "end": v(-12.87, 1.47) * mm});
            skArc(sketch, "E12.3.0.0", {"start": v(-6.37, 18.57) * mm, "mid": v(-7.52, 16.52) * mm, "end": v(-6.37, 14.47) * mm});
            skLineSegment(sketch, "E12.3.0.1", {"start": v(-3.88, 18.57) * mm, "end": v(-6.37, 18.57) * mm});
            skArc(sketch, "E12.3.0.2", {"start": v(-3.88, 14.47) * mm, "mid": v(-2.72, 16.52) * mm, "end": v(-3.88, 18.57) * mm});
            skLineSegment(sketch, "E12.3.0.3", {"start": v(-3.88, 14.47) * mm, "end": v(-6.37, 14.47) * mm});
            skArc(sketch, "E12.3.1.0", {"start": v(-6.37, 12.07) * mm, "mid": v(-7.52, 10.02) * mm, "end": v(-6.37, 7.97) * mm});
            skLineSegment(sketch, "E12.3.1.1", {"start": v(-3.88, 12.07) * mm, "end": v(-6.37, 12.07) * mm});
            skArc(sketch, "E12.3.1.2", {"start": v(-3.88, 7.97) * mm, "mid": v(-2.72, 10.02) * mm, "end": v(-3.88, 12.07) * mm});
            skLineSegment(sketch, "E12.3.1.3", {"start": v(-3.88, 7.97) * mm, "end": v(-6.37, 7.97) * mm});
            skArc(sketch, "E12.3.2.0", {"start": v(-6.37, 5.57) * mm, "mid": v(-7.52, 3.52) * mm, "end": v(-6.37, 1.47) * mm});
            skLineSegment(sketch, "E12.3.2.1", {"start": v(-3.88, 5.57) * mm, "end": v(-6.37, 5.57) * mm});
            skArc(sketch, "E12.3.2.2", {"start": v(-3.88, 1.47) * mm, "mid": v(-2.72, 3.52) * mm, "end": v(-3.88, 5.57) * mm});
            skLineSegment(sketch, "E12.3.2.3", {"start": v(-3.88, 1.47) * mm, "end": v(-6.37, 1.47) * mm});
            skLineSegment(sketch, "E12.direction1", {"start": v(-25.87, 14.47) * mm, "end": v(-19.37, 14.47) * mm, "construction": true});
            skLineSegment(sketch, "E12.direction2", {"start": v(-25.87, 14.47) * mm, "end": v(-25.87, 7.97) * mm, "construction": true});
            skLineSegment(sketch, "E13.bottom", {"start": v(-29.32, 20.87) * mm, "end": v(19.08, 20.87) * mm});
            skLineSegment(sketch, "E13.top", {"start": v(-29.32, -26.83) * mm, "end": v(19.08, -26.83) * mm});
            skLineSegment(sketch, "E13.left", {"start": v(-29.32, 20.87) * mm, "end": v(-29.32, -26.83) * mm});
            skLineSegment(sketch, "E13.right", {"start": v(19.08, 20.87) * mm, "end": v(19.08, -26.83) * mm});
            skArc(sketch, "E14.0.4.0", {"start": v(0.13, 18.57) * mm, "mid": v(-1.02, 16.52) * mm, "end": v(0.13, 14.47) * mm});
            skLineSegment(sketch, "E14.4.4.0", {"start": v(2.62, 18.57) * mm, "end": v(0.13, 18.57) * mm});
            skArc(sketch, "E14.7.4.0", {"start": v(2.62, 14.47) * mm, "mid": v(3.78, 16.52) * mm, "end": v(2.62, 18.57) * mm});
            skLineSegment(sketch, "E14.11.4.0", {"start": v(2.62, 14.47) * mm, "end": v(0.13, 14.47) * mm});
            skArc(sketch, "E14.0.4.1", {"start": v(0.13, 12.07) * mm, "mid": v(-1.02, 10.02) * mm, "end": v(0.13, 7.97) * mm});
            skLineSegment(sketch, "E14.4.4.1", {"start": v(2.62, 12.07) * mm, "end": v(0.13, 12.07) * mm});
            skArc(sketch, "E14.7.4.1", {"start": v(2.62, 7.97) * mm, "mid": v(3.78, 10.02) * mm, "end": v(2.62, 12.07) * mm});
            skLineSegment(sketch, "E14.11.4.1", {"start": v(2.62, 7.97) * mm, "end": v(0.13, 7.97) * mm});
            skArc(sketch, "E14.0.4.2", {"start": v(0.13, 5.57) * mm, "mid": v(-1.02, 3.52) * mm, "end": v(0.13, 1.47) * mm});
            skLineSegment(sketch, "E14.4.4.2", {"start": v(2.62, 5.57) * mm, "end": v(0.13, 5.57) * mm});
            skArc(sketch, "E14.7.4.2", {"start": v(2.62, 1.47) * mm, "mid": v(3.78, 3.52) * mm, "end": v(2.62, 5.57) * mm});
            skLineSegment(sketch, "E14.11.4.2", {"start": v(2.62, 1.47) * mm, "end": v(0.13, 1.47) * mm});
            skArc(sketch, "E14.0.5.0", {"start": v(6.63, 18.57) * mm, "mid": v(5.48, 16.52) * mm, "end": v(6.63, 14.47) * mm});
            skLineSegment(sketch, "E14.4.5.0", {"start": v(9.12, 18.57) * mm, "end": v(6.63, 18.57) * mm});
            skArc(sketch, "E14.7.5.0", {"start": v(9.12, 14.47) * mm, "mid": v(10.28, 16.52) * mm, "end": v(9.12, 18.57) * mm});
            skLineSegment(sketch, "E14.11.5.0", {"start": v(9.12, 14.47) * mm, "end": v(6.63, 14.47) * mm});
            skArc(sketch, "E14.0.5.1", {"start": v(6.63, 12.07) * mm, "mid": v(5.48, 10.02) * mm, "end": v(6.63, 7.97) * mm});
            skLineSegment(sketch, "E14.4.5.1", {"start": v(9.12, 12.07) * mm, "end": v(6.63, 12.07) * mm});
            skArc(sketch, "E14.7.5.1", {"start": v(9.12, 7.97) * mm, "mid": v(10.28, 10.02) * mm, "end": v(9.12, 12.07) * mm});
            skLineSegment(sketch, "E14.11.5.1", {"start": v(9.12, 7.97) * mm, "end": v(6.63, 7.97) * mm});
            skArc(sketch, "E14.0.5.2", {"start": v(6.63, 5.57) * mm, "mid": v(5.48, 3.52) * mm, "end": v(6.63, 1.47) * mm});
            skLineSegment(sketch, "E14.4.5.2", {"start": v(9.12, 5.57) * mm, "end": v(6.63, 5.57) * mm});
            skArc(sketch, "E14.7.5.2", {"start": v(9.12, 1.47) * mm, "mid": v(10.28, 3.52) * mm, "end": v(9.12, 5.57) * mm});
            skLineSegment(sketch, "E14.11.5.2", {"start": v(9.12, 1.47) * mm, "end": v(6.63, 1.47) * mm});
            skArc(sketch, "E14.0.6.0", {"start": v(13.13, 18.57) * mm, "mid": v(11.98, 16.52) * mm, "end": v(13.13, 14.47) * mm});
            skLineSegment(sketch, "E14.4.6.0", {"start": v(15.62, 18.57) * mm, "end": v(13.13, 18.57) * mm});
            skArc(sketch, "E14.7.6.0", {"start": v(15.62, 14.47) * mm, "mid": v(16.78, 16.52) * mm, "end": v(15.62, 18.57) * mm});
            skLineSegment(sketch, "E14.11.6.0", {"start": v(15.62, 14.47) * mm, "end": v(13.13, 14.47) * mm});
            skArc(sketch, "E14.0.6.1", {"start": v(13.13, 12.07) * mm, "mid": v(11.98, 10.02) * mm, "end": v(13.13, 7.97) * mm});
            skLineSegment(sketch, "E14.4.6.1", {"start": v(15.62, 12.07) * mm, "end": v(13.13, 12.07) * mm});
            skArc(sketch, "E14.7.6.1", {"start": v(15.62, 7.97) * mm, "mid": v(16.78, 10.02) * mm, "end": v(15.62, 12.07) * mm});
            skLineSegment(sketch, "E14.11.6.1", {"start": v(15.62, 7.97) * mm, "end": v(13.13, 7.97) * mm});
            skArc(sketch, "E14.0.6.2", {"start": v(13.13, 5.57) * mm, "mid": v(11.98, 3.52) * mm, "end": v(13.13, 1.47) * mm});
            skLineSegment(sketch, "E14.4.6.2", {"start": v(15.62, 5.57) * mm, "end": v(13.13, 5.57) * mm});
            skArc(sketch, "E14.7.6.2", {"start": v(15.62, 1.47) * mm, "mid": v(16.78, 3.52) * mm, "end": v(15.62, 5.57) * mm});
            skLineSegment(sketch, "E14.11.6.2", {"start": v(15.62, 1.47) * mm, "end": v(13.13, 1.47) * mm});
            skArc(sketch, "E15.0.0.3", {"start": v(-25.87, -0.93) * mm, "mid": v(-27.02, -2.98) * mm, "end": v(-25.87, -5.03) * mm});
            skLineSegment(sketch, "E15.4.0.3", {"start": v(-23.38, -0.93) * mm, "end": v(-25.87, -0.93) * mm});
            skArc(sketch, "E15.7.0.3", {"start": v(-23.38, -5.03) * mm, "mid": v(-22.22, -2.98) * mm, "end": v(-23.38, -0.93) * mm});
            skLineSegment(sketch, "E15.11.0.3", {"start": v(-23.38, -5.03) * mm, "end": v(-25.87, -5.03) * mm});
            skArc(sketch, "E15.0.0.4", {"start": v(-25.87, -7.43) * mm, "mid": v(-27.02, -9.48) * mm, "end": v(-25.87, -11.53) * mm});
            skLineSegment(sketch, "E15.4.0.4", {"start": v(-23.38, -7.43) * mm, "end": v(-25.87, -7.43) * mm});
            skArc(sketch, "E15.7.0.4", {"start": v(-23.38, -11.53) * mm, "mid": v(-22.22, -9.48) * mm, "end": v(-23.38, -7.43) * mm});
            skLineSegment(sketch, "E15.11.0.4", {"start": v(-23.38, -11.53) * mm, "end": v(-25.87, -11.53) * mm});
            skArc(sketch, "E15.0.0.5", {"start": v(-25.87, -13.93) * mm, "mid": v(-27.02, -15.98) * mm, "end": v(-25.87, -18.03) * mm});
            skLineSegment(sketch, "E15.4.0.5", {"start": v(-23.38, -13.93) * mm, "end": v(-25.87, -13.93) * mm});
            skArc(sketch, "E15.7.0.5", {"start": v(-23.38, -18.03) * mm, "mid": v(-22.22, -15.98) * mm, "end": v(-23.38, -13.93) * mm});
            skLineSegment(sketch, "E15.11.0.5", {"start": v(-23.38, -18.03) * mm, "end": v(-25.87, -18.03) * mm});
            skArc(sketch, "E15.0.0.6", {"start": v(-25.87, -20.43) * mm, "mid": v(-27.02, -22.48) * mm, "end": v(-25.87, -24.53) * mm});
            skLineSegment(sketch, "E15.4.0.6", {"start": v(-23.38, -20.43) * mm, "end": v(-25.87, -20.43) * mm});
            skArc(sketch, "E15.7.0.6", {"start": v(-23.38, -24.53) * mm, "mid": v(-22.22, -22.48) * mm, "end": v(-23.38, -20.43) * mm});
            skLineSegment(sketch, "E15.11.0.6", {"start": v(-23.38, -24.53) * mm, "end": v(-25.87, -24.53) * mm});
            skArc(sketch, "E15.0.1.3", {"start": v(-19.37, -0.93) * mm, "mid": v(-20.52, -2.98) * mm, "end": v(-19.37, -5.03) * mm});
            skLineSegment(sketch, "E15.4.1.3", {"start": v(-16.88, -0.93) * mm, "end": v(-19.37, -0.93) * mm});
            skArc(sketch, "E15.7.1.3", {"start": v(-16.88, -5.03) * mm, "mid": v(-15.72, -2.98) * mm, "end": v(-16.88, -0.93) * mm});
            skLineSegment(sketch, "E15.11.1.3", {"start": v(-16.88, -5.03) * mm, "end": v(-19.37, -5.03) * mm});
            skArc(sketch, "E15.0.1.4", {"start": v(-19.37, -7.43) * mm, "mid": v(-20.52, -9.48) * mm, "end": v(-19.37, -11.53) * mm});
            skLineSegment(sketch, "E15.4.1.4", {"start": v(-16.88, -7.43) * mm, "end": v(-19.37, -7.43) * mm});
            skArc(sketch, "E15.7.1.4", {"start": v(-16.88, -11.53) * mm, "mid": v(-15.72, -9.48) * mm, "end": v(-16.88, -7.43) * mm});
            skLineSegment(sketch, "E15.11.1.4", {"start": v(-16.88, -11.53) * mm, "end": v(-19.37, -11.53) * mm});
            skArc(sketch, "E15.0.1.5", {"start": v(-19.37, -13.93) * mm, "mid": v(-20.52, -15.98) * mm, "end": v(-19.37, -18.03) * mm});
            skLineSegment(sketch, "E15.4.1.5", {"start": v(-16.88, -13.93) * mm, "end": v(-19.37, -13.93) * mm});
            skArc(sketch, "E15.7.1.5", {"start": v(-16.88, -18.03) * mm, "mid": v(-15.72, -15.98) * mm, "end": v(-16.88, -13.93) * mm});
            skLineSegment(sketch, "E15.11.1.5", {"start": v(-16.88, -18.03) * mm, "end": v(-19.37, -18.03) * mm});
            skArc(sketch, "E15.0.1.6", {"start": v(-19.37, -20.43) * mm, "mid": v(-20.52, -22.48) * mm, "end": v(-19.37, -24.53) * mm});
            skLineSegment(sketch, "E15.4.1.6", {"start": v(-16.88, -20.43) * mm, "end": v(-19.37, -20.43) * mm});
            skArc(sketch, "E15.7.1.6", {"start": v(-16.88, -24.53) * mm, "mid": v(-15.72, -22.48) * mm, "end": v(-16.88, -20.43) * mm});
            skLineSegment(sketch, "E15.11.1.6", {"start": v(-16.88, -24.53) * mm, "end": v(-19.37, -24.53) * mm});
            skArc(sketch, "E15.0.2.3", {"start": v(-12.87, -0.93) * mm, "mid": v(-14.02, -2.98) * mm, "end": v(-12.87, -5.03) * mm});
            skLineSegment(sketch, "E15.4.2.3", {"start": v(-10.38, -0.93) * mm, "end": v(-12.87, -0.93) * mm});
            skArc(sketch, "E15.7.2.3", {"start": v(-10.38, -5.03) * mm, "mid": v(-9.22, -2.98) * mm, "end": v(-10.38, -0.93) * mm});
            skLineSegment(sketch, "E15.11.2.3", {"start": v(-10.38, -5.03) * mm, "end": v(-12.87, -5.03) * mm});
            skArc(sketch, "E15.0.2.4", {"start": v(-12.87, -7.43) * mm, "mid": v(-14.02, -9.48) * mm, "end": v(-12.87, -11.53) * mm});
            skLineSegment(sketch, "E15.4.2.4", {"start": v(-10.38, -7.43) * mm, "end": v(-12.87, -7.43) * mm});
            skArc(sketch, "E15.7.2.4", {"start": v(-10.38, -11.53) * mm, "mid": v(-9.22, -9.48) * mm, "end": v(-10.38, -7.43) * mm});
            skLineSegment(sketch, "E15.11.2.4", {"start": v(-10.38, -11.53) * mm, "end": v(-12.87, -11.53) * mm});
            skArc(sketch, "E15.0.2.5", {"start": v(-12.87, -13.93) * mm, "mid": v(-14.02, -15.98) * mm, "end": v(-12.87, -18.03) * mm});
            skLineSegment(sketch, "E15.4.2.5", {"start": v(-10.38, -13.93) * mm, "end": v(-12.87, -13.93) * mm});
            skArc(sketch, "E15.7.2.5", {"start": v(-10.38, -18.03) * mm, "mid": v(-9.22, -15.98) * mm, "end": v(-10.38, -13.93) * mm});
            skLineSegment(sketch, "E15.11.2.5", {"start": v(-10.38, -18.03) * mm, "end": v(-12.87, -18.03) * mm});
            skArc(sketch, "E15.0.2.6", {"start": v(-12.87, -20.43) * mm, "mid": v(-14.02, -22.48) * mm, "end": v(-12.87, -24.53) * mm});
            skLineSegment(sketch, "E15.4.2.6", {"start": v(-10.38, -20.43) * mm, "end": v(-12.87, -20.43) * mm});
            skArc(sketch, "E15.7.2.6", {"start": v(-10.38, -24.53) * mm, "mid": v(-9.22, -22.48) * mm, "end": v(-10.38, -20.43) * mm});
            skLineSegment(sketch, "E15.11.2.6", {"start": v(-10.38, -24.53) * mm, "end": v(-12.87, -24.53) * mm});
            skArc(sketch, "E15.0.3.3", {"start": v(-6.37, -0.93) * mm, "mid": v(-7.52, -2.98) * mm, "end": v(-6.37, -5.03) * mm});
            skLineSegment(sketch, "E15.4.3.3", {"start": v(-3.88, -0.93) * mm, "end": v(-6.37, -0.93) * mm});
            skArc(sketch, "E15.7.3.3", {"start": v(-3.88, -5.03) * mm, "mid": v(-2.72, -2.98) * mm, "end": v(-3.88, -0.93) * mm});
            skLineSegment(sketch, "E15.11.3.3", {"start": v(-3.88, -5.03) * mm, "end": v(-6.37, -5.03) * mm});
            skArc(sketch, "E15.0.3.4", {"start": v(-6.37, -7.43) * mm, "mid": v(-7.52, -9.48) * mm, "end": v(-6.37, -11.53) * mm});
            skLineSegment(sketch, "E15.4.3.4", {"start": v(-3.88, -7.43) * mm, "end": v(-6.37, -7.43) * mm});
            skArc(sketch, "E15.7.3.4", {"start": v(-3.88, -11.53) * mm, "mid": v(-2.72, -9.48) * mm, "end": v(-3.88, -7.43) * mm});
            skLineSegment(sketch, "E15.11.3.4", {"start": v(-3.88, -11.53) * mm, "end": v(-6.37, -11.53) * mm});
            skArc(sketch, "E15.0.3.5", {"start": v(-6.37, -13.93) * mm, "mid": v(-7.52, -15.98) * mm, "end": v(-6.37, -18.03) * mm});
            skLineSegment(sketch, "E15.4.3.5", {"start": v(-3.88, -13.93) * mm, "end": v(-6.37, -13.93) * mm});
            skArc(sketch, "E15.7.3.5", {"start": v(-3.88, -18.03) * mm, "mid": v(-2.72, -15.98) * mm, "end": v(-3.88, -13.93) * mm});
            skLineSegment(sketch, "E15.11.3.5", {"start": v(-3.88, -18.03) * mm, "end": v(-6.37, -18.03) * mm});
            skArc(sketch, "E15.0.3.6", {"start": v(-6.37, -20.43) * mm, "mid": v(-7.52, -22.48) * mm, "end": v(-6.37, -24.53) * mm});
            skLineSegment(sketch, "E15.4.3.6", {"start": v(-3.88, -20.43) * mm, "end": v(-6.37, -20.43) * mm});
            skArc(sketch, "E15.7.3.6", {"start": v(-3.88, -24.53) * mm, "mid": v(-2.72, -22.48) * mm, "end": v(-3.88, -20.43) * mm});
            skLineSegment(sketch, "E15.11.3.6", {"start": v(-3.88, -24.53) * mm, "end": v(-6.37, -24.53) * mm});
            skArc(sketch, "E15.0.4.3", {"start": v(0.13, -0.93) * mm, "mid": v(-1.02, -2.98) * mm, "end": v(0.13, -5.03) * mm});
            skLineSegment(sketch, "E15.4.4.3", {"start": v(2.62, -0.93) * mm, "end": v(0.13, -0.93) * mm});
            skArc(sketch, "E15.7.4.3", {"start": v(2.62, -5.03) * mm, "mid": v(3.78, -2.98) * mm, "end": v(2.62, -0.93) * mm});
            skLineSegment(sketch, "E15.11.4.3", {"start": v(2.62, -5.03) * mm, "end": v(0.13, -5.03) * mm});
            skArc(sketch, "E15.0.4.4", {"start": v(0.13, -7.43) * mm, "mid": v(-1.02, -9.48) * mm, "end": v(0.13, -11.53) * mm});
            skLineSegment(sketch, "E15.4.4.4", {"start": v(2.62, -7.43) * mm, "end": v(0.13, -7.43) * mm});
            skArc(sketch, "E15.7.4.4", {"start": v(2.62, -11.53) * mm, "mid": v(3.78, -9.48) * mm, "end": v(2.62, -7.43) * mm});
            skLineSegment(sketch, "E15.11.4.4", {"start": v(2.62, -11.53) * mm, "end": v(0.13, -11.53) * mm});
            skArc(sketch, "E15.0.4.5", {"start": v(0.13, -13.93) * mm, "mid": v(-1.02, -15.98) * mm, "end": v(0.13, -18.03) * mm});
            skLineSegment(sketch, "E15.4.4.5", {"start": v(2.62, -13.93) * mm, "end": v(0.13, -13.93) * mm});
            skArc(sketch, "E15.7.4.5", {"start": v(2.62, -18.03) * mm, "mid": v(3.78, -15.98) * mm, "end": v(2.62, -13.93) * mm});
            skLineSegment(sketch, "E15.11.4.5", {"start": v(2.62, -18.03) * mm, "end": v(0.13, -18.03) * mm});
            skArc(sketch, "E15.0.4.6", {"start": v(0.13, -20.43) * mm, "mid": v(-1.02, -22.48) * mm, "end": v(0.13, -24.53) * mm});
            skLineSegment(sketch, "E15.4.4.6", {"start": v(2.62, -20.43) * mm, "end": v(0.13, -20.43) * mm});
            skArc(sketch, "E15.7.4.6", {"start": v(2.62, -24.53) * mm, "mid": v(3.78, -22.48) * mm, "end": v(2.62, -20.43) * mm});
            skLineSegment(sketch, "E15.11.4.6", {"start": v(2.62, -24.53) * mm, "end": v(0.13, -24.53) * mm});
            skArc(sketch, "E15.0.5.3", {"start": v(6.63, -0.93) * mm, "mid": v(5.48, -2.98) * mm, "end": v(6.63, -5.03) * mm});
            skLineSegment(sketch, "E15.4.5.3", {"start": v(9.12, -0.93) * mm, "end": v(6.63, -0.93) * mm});
            skArc(sketch, "E15.7.5.3", {"start": v(9.12, -5.03) * mm, "mid": v(10.28, -2.98) * mm, "end": v(9.12, -0.93) * mm});
            skLineSegment(sketch, "E15.11.5.3", {"start": v(9.12, -5.03) * mm, "end": v(6.63, -5.03) * mm});
            skArc(sketch, "E15.0.5.4", {"start": v(6.63, -7.43) * mm, "mid": v(5.48, -9.48) * mm, "end": v(6.63, -11.53) * mm});
            skLineSegment(sketch, "E15.4.5.4", {"start": v(9.12, -7.43) * mm, "end": v(6.63, -7.43) * mm});
            skArc(sketch, "E15.7.5.4", {"start": v(9.12, -11.53) * mm, "mid": v(10.28, -9.48) * mm, "end": v(9.12, -7.43) * mm});
            skLineSegment(sketch, "E15.11.5.4", {"start": v(9.12, -11.53) * mm, "end": v(6.63, -11.53) * mm});
            skArc(sketch, "E15.0.5.5", {"start": v(6.63, -13.93) * mm, "mid": v(5.48, -15.98) * mm, "end": v(6.63, -18.03) * mm});
            skLineSegment(sketch, "E15.4.5.5", {"start": v(9.12, -13.93) * mm, "end": v(6.63, -13.93) * mm});
            skArc(sketch, "E15.7.5.5", {"start": v(9.12, -18.03) * mm, "mid": v(10.28, -15.98) * mm, "end": v(9.12, -13.93) * mm});
            skLineSegment(sketch, "E15.11.5.5", {"start": v(9.12, -18.03) * mm, "end": v(6.63, -18.03) * mm});
            skArc(sketch, "E15.0.5.6", {"start": v(6.63, -20.43) * mm, "mid": v(5.48, -22.48) * mm, "end": v(6.63, -24.53) * mm});
            skLineSegment(sketch, "E15.4.5.6", {"start": v(9.12, -20.43) * mm, "end": v(6.63, -20.43) * mm});
            skArc(sketch, "E15.7.5.6", {"start": v(9.12, -24.53) * mm, "mid": v(10.28, -22.48) * mm, "end": v(9.12, -20.43) * mm});
            skLineSegment(sketch, "E15.11.5.6", {"start": v(9.12, -24.53) * mm, "end": v(6.63, -24.53) * mm});
            skArc(sketch, "E15.0.6.3", {"start": v(13.13, -0.93) * mm, "mid": v(11.98, -2.98) * mm, "end": v(13.13, -5.03) * mm});
            skLineSegment(sketch, "E15.4.6.3", {"start": v(15.62, -0.93) * mm, "end": v(13.13, -0.93) * mm});
            skArc(sketch, "E15.7.6.3", {"start": v(15.62, -5.03) * mm, "mid": v(16.78, -2.98) * mm, "end": v(15.62, -0.93) * mm});
            skLineSegment(sketch, "E15.11.6.3", {"start": v(15.62, -5.03) * mm, "end": v(13.13, -5.03) * mm});
            skArc(sketch, "E15.0.6.4", {"start": v(13.13, -7.43) * mm, "mid": v(11.98, -9.48) * mm, "end": v(13.13, -11.53) * mm});
            skLineSegment(sketch, "E15.4.6.4", {"start": v(15.62, -7.43) * mm, "end": v(13.13, -7.43) * mm});
            skArc(sketch, "E15.7.6.4", {"start": v(15.62, -11.53) * mm, "mid": v(16.78, -9.48) * mm, "end": v(15.62, -7.43) * mm});
            skLineSegment(sketch, "E15.11.6.4", {"start": v(15.62, -11.53) * mm, "end": v(13.13, -11.53) * mm});
            skArc(sketch, "E15.0.6.5", {"start": v(13.13, -13.93) * mm, "mid": v(11.98, -15.98) * mm, "end": v(13.13, -18.03) * mm});
            skLineSegment(sketch, "E15.4.6.5", {"start": v(15.62, -13.93) * mm, "end": v(13.13, -13.93) * mm});
            skArc(sketch, "E15.7.6.5", {"start": v(15.62, -18.03) * mm, "mid": v(16.78, -15.98) * mm, "end": v(15.62, -13.93) * mm});
            skLineSegment(sketch, "E15.11.6.5", {"start": v(15.62, -18.03) * mm, "end": v(13.13, -18.03) * mm});
            skArc(sketch, "E15.0.6.6", {"start": v(13.13, -20.43) * mm, "mid": v(11.98, -22.48) * mm, "end": v(13.13, -24.53) * mm});
            skLineSegment(sketch, "E15.4.6.6", {"start": v(15.62, -20.43) * mm, "end": v(13.13, -20.43) * mm});
            skArc(sketch, "E15.7.6.6", {"start": v(15.62, -24.53) * mm, "mid": v(16.78, -22.48) * mm, "end": v(15.62, -20.43) * mm});
            skLineSegment(sketch, "E15.11.6.6", {"start": v(15.62, -24.53) * mm, "end": v(13.13, -24.53) * mm});
            skSolve(sketch);
        }
        {
            var Q0;
            Q0=qSketchRegion(id+"F2",true);
            extrude(context, id + "F3", {"entities" : qUnion([Q0]), "operationType" : NewBodyOperationType.ADD, "depth" : 0.3 * mm});
        }
        {
            var Q0;
            Q0=makeQuery(id+"F0.imprint","IMPRINT",FACE,{"disambiguationData":[TD([[makeQuery(id+"F0.imprint","IMPRINT",EDGE,{"derivedFrom":sQuery(id+"F0.wireOp",EDGE,"E1")}),-1.0]])]});
            var sketch = newSketch(context, id + "F4", { "sketchPlane" : qUnion([Q0])});
            skArc(sketch, "E16.0", {"start": v(-25.87, 5.57) * mm, "mid": v(-27.02, 3.52) * mm, "end": v(-25.87, 1.47) * mm});
            skLineSegment(sketch, "E16.1", {"start": v(-23.38, 5.57) * mm, "end": v(-25.87, 5.57) * mm});
            skArc(sketch, "E16.2", {"start": v(-23.38, 1.47) * mm, "mid": v(-22.22, 3.52) * mm, "end": v(-23.38, 5.57) * mm});
            skLineSegment(sketch, "E16.3", {"start": v(-23.38, 1.47) * mm, "end": v(-25.87, 1.47) * mm});
            skArc(sketch, "E17.0.1.0", {"start": v(-23.38, 7.97) * mm, "mid": v(-22.22, 10.02) * mm, "end": v(-23.38, 12.07) * mm});
            skLineSegment(sketch, "E17.0.1.1", {"start": v(-23.38, 7.97) * mm, "end": v(-25.87, 7.97) * mm});
            skArc(sketch, "E17.0.1.2", {"start": v(-25.87, 12.07) * mm, "mid": v(-27.02, 10.02) * mm, "end": v(-25.87, 7.97) * mm});
            skLineSegment(sketch, "E17.0.1.3", {"start": v(-23.38, 12.07) * mm, "end": v(-25.87, 12.07) * mm});
            skArc(sketch, "E17.0.2.0", {"start": v(-23.38, 14.47) * mm, "mid": v(-22.22, 16.52) * mm, "end": v(-23.38, 18.57) * mm});
            skLineSegment(sketch, "E17.0.2.1", {"start": v(-23.38, 14.47) * mm, "end": v(-25.87, 14.47) * mm});
            skArc(sketch, "E17.0.2.2", {"start": v(-25.87, 18.57) * mm, "mid": v(-27.02, 16.52) * mm, "end": v(-25.87, 14.47) * mm});
            skLineSegment(sketch, "E17.0.2.3", {"start": v(-23.38, 18.57) * mm, "end": v(-25.87, 18.57) * mm});
            skArc(sketch, "E17.1.0.0", {"start": v(-16.88, 1.47) * mm, "mid": v(-15.72, 3.52) * mm, "end": v(-16.88, 5.57) * mm});
            skLineSegment(sketch, "E17.1.0.1", {"start": v(-16.88, 1.47) * mm, "end": v(-19.37, 1.47) * mm});
            skArc(sketch, "E17.1.0.2", {"start": v(-19.37, 5.57) * mm, "mid": v(-20.52, 3.52) * mm, "end": v(-19.37, 1.47) * mm});
            skLineSegment(sketch, "E17.1.0.3", {"start": v(-16.88, 5.57) * mm, "end": v(-19.37, 5.57) * mm});
            skArc(sketch, "E17.1.1.0", {"start": v(-16.88, 7.97) * mm, "mid": v(-15.72, 10.02) * mm, "end": v(-16.88, 12.07) * mm});
            skLineSegment(sketch, "E17.1.1.1", {"start": v(-16.88, 7.97) * mm, "end": v(-19.37, 7.97) * mm});
            skArc(sketch, "E17.1.1.2", {"start": v(-19.37, 12.07) * mm, "mid": v(-20.52, 10.02) * mm, "end": v(-19.37, 7.97) * mm});
            skLineSegment(sketch, "E17.1.1.3", {"start": v(-16.88, 12.07) * mm, "end": v(-19.37, 12.07) * mm});
            skArc(sketch, "E17.1.2.0", {"start": v(-16.88, 14.47) * mm, "mid": v(-15.72, 16.52) * mm, "end": v(-16.88, 18.57) * mm});
            skLineSegment(sketch, "E17.1.2.1", {"start": v(-16.88, 14.47) * mm, "end": v(-19.37, 14.47) * mm});
            skArc(sketch, "E17.1.2.2", {"start": v(-19.37, 18.57) * mm, "mid": v(-20.52, 16.52) * mm, "end": v(-19.37, 14.47) * mm});
            skLineSegment(sketch, "E17.1.2.3", {"start": v(-16.88, 18.57) * mm, "end": v(-19.37, 18.57) * mm});
            skArc(sketch, "E17.2.0.0", {"start": v(-10.38, 1.47) * mm, "mid": v(-9.22, 3.52) * mm, "end": v(-10.38, 5.57) * mm});
            skLineSegment(sketch, "E17.2.0.1", {"start": v(-10.38, 1.47) * mm, "end": v(-12.87, 1.47) * mm});
            skArc(sketch, "E17.2.0.2", {"start": v(-12.87, 5.57) * mm, "mid": v(-14.02, 3.52) * mm, "end": v(-12.87, 1.47) * mm});
            skLineSegment(sketch, "E17.2.0.3", {"start": v(-10.38, 5.57) * mm, "end": v(-12.87, 5.57) * mm});
            skArc(sketch, "E17.2.1.0", {"start": v(-10.38, 7.97) * mm, "mid": v(-9.22, 10.02) * mm, "end": v(-10.38, 12.07) * mm});
            skLineSegment(sketch, "E17.2.1.1", {"start": v(-10.38, 7.97) * mm, "end": v(-12.87, 7.97) * mm});
            skArc(sketch, "E17.2.1.2", {"start": v(-12.87, 12.07) * mm, "mid": v(-14.02, 10.02) * mm, "end": v(-12.87, 7.97) * mm});
            skLineSegment(sketch, "E17.2.1.3", {"start": v(-10.38, 12.07) * mm, "end": v(-12.87, 12.07) * mm});
            skArc(sketch, "E17.2.2.0", {"start": v(-10.38, 14.47) * mm, "mid": v(-9.22, 16.52) * mm, "end": v(-10.38, 18.57) * mm});
            skLineSegment(sketch, "E17.2.2.1", {"start": v(-10.38, 14.47) * mm, "end": v(-12.87, 14.47) * mm});
            skArc(sketch, "E17.2.2.2", {"start": v(-12.87, 18.57) * mm, "mid": v(-14.02, 16.52) * mm, "end": v(-12.87, 14.47) * mm});
            skLineSegment(sketch, "E17.2.2.3", {"start": v(-10.38, 18.57) * mm, "end": v(-12.87, 18.57) * mm});
            skArc(sketch, "E17.3.0.0", {"start": v(-3.88, 1.47) * mm, "mid": v(-2.72, 3.52) * mm, "end": v(-3.88, 5.57) * mm});
            skLineSegment(sketch, "E17.3.0.1", {"start": v(-3.88, 1.47) * mm, "end": v(-6.37, 1.47) * mm});
            skArc(sketch, "E17.3.0.2", {"start": v(-6.37, 5.57) * mm, "mid": v(-7.52, 3.52) * mm, "end": v(-6.37, 1.47) * mm});
            skLineSegment(sketch, "E17.3.0.3", {"start": v(-3.88, 5.57) * mm, "end": v(-6.37, 5.57) * mm});
            skArc(sketch, "E17.3.1.0", {"start": v(-3.88, 7.97) * mm, "mid": v(-2.72, 10.02) * mm, "end": v(-3.88, 12.07) * mm});
            skLineSegment(sketch, "E17.3.1.1", {"start": v(-3.88, 7.97) * mm, "end": v(-6.37, 7.97) * mm});
            skArc(sketch, "E17.3.1.2", {"start": v(-6.37, 12.07) * mm, "mid": v(-7.52, 10.02) * mm, "end": v(-6.37, 7.97) * mm});
            skLineSegment(sketch, "E17.3.1.3", {"start": v(-3.88, 12.07) * mm, "end": v(-6.37, 12.07) * mm});
            skArc(sketch, "E17.3.2.0", {"start": v(-3.88, 14.47) * mm, "mid": v(-2.72, 16.52) * mm, "end": v(-3.88, 18.57) * mm});
            skLineSegment(sketch, "E17.3.2.1", {"start": v(-3.88, 14.47) * mm, "end": v(-6.37, 14.47) * mm});
            skArc(sketch, "E17.3.2.2", {"start": v(-6.37, 18.57) * mm, "mid": v(-7.52, 16.52) * mm, "end": v(-6.37, 14.47) * mm});
            skLineSegment(sketch, "E17.3.2.3", {"start": v(-3.88, 18.57) * mm, "end": v(-6.37, 18.57) * mm});
            skLineSegment(sketch, "E17.direction1", {"start": v(-25.87, 1.47) * mm, "end": v(-19.37, 1.47) * mm, "construction": true});
            skLineSegment(sketch, "E17.direction2", {"start": v(-25.87, 1.47) * mm, "end": v(-25.87, 7.97) * mm, "construction": true});
            skLineSegment(sketch, "E18.bottom", {"start": v(-29.32, -26.83) * mm, "end": v(19.08, -26.83) * mm});
            skLineSegment(sketch, "E18.top", {"start": v(-29.32, 20.87) * mm, "end": v(19.08, 20.87) * mm});
            skLineSegment(sketch, "E18.left", {"start": v(-29.32, -26.83) * mm, "end": v(-29.32, 20.87) * mm});
            skLineSegment(sketch, "E18.right", {"start": v(19.08, -26.83) * mm, "end": v(19.08, 20.87) * mm});
            skArc(sketch, "E19.0.4.0", {"start": v(2.62, 1.47) * mm, "mid": v(3.78, 3.52) * mm, "end": v(2.62, 5.57) * mm});
            skLineSegment(sketch, "E19.4.4.0", {"start": v(2.62, 1.47) * mm, "end": v(0.13, 1.47) * mm});
            skArc(sketch, "E19.7.4.0", {"start": v(0.13, 5.57) * mm, "mid": v(-1.02, 3.52) * mm, "end": v(0.13, 1.47) * mm});
            skLineSegment(sketch, "E19.11.4.0", {"start": v(2.62, 5.57) * mm, "end": v(0.13, 5.57) * mm});
            skArc(sketch, "E19.0.4.1", {"start": v(2.62, 7.97) * mm, "mid": v(3.78, 10.02) * mm, "end": v(2.62, 12.07) * mm});
            skLineSegment(sketch, "E19.4.4.1", {"start": v(2.62, 7.97) * mm, "end": v(0.13, 7.97) * mm});
            skArc(sketch, "E19.7.4.1", {"start": v(0.13, 12.07) * mm, "mid": v(-1.02, 10.02) * mm, "end": v(0.13, 7.97) * mm});
            skLineSegment(sketch, "E19.11.4.1", {"start": v(2.62, 12.07) * mm, "end": v(0.13, 12.07) * mm});
            skArc(sketch, "E19.0.4.2", {"start": v(2.62, 14.47) * mm, "mid": v(3.78, 16.52) * mm, "end": v(2.62, 18.57) * mm});
            skLineSegment(sketch, "E19.4.4.2", {"start": v(2.62, 14.47) * mm, "end": v(0.13, 14.47) * mm});
            skArc(sketch, "E19.7.4.2", {"start": v(0.13, 18.57) * mm, "mid": v(-1.02, 16.52) * mm, "end": v(0.13, 14.47) * mm});
            skLineSegment(sketch, "E19.11.4.2", {"start": v(2.62, 18.57) * mm, "end": v(0.13, 18.57) * mm});
            skArc(sketch, "E19.0.5.0", {"start": v(9.12, 1.47) * mm, "mid": v(10.28, 3.52) * mm, "end": v(9.12, 5.57) * mm});
            skLineSegment(sketch, "E19.4.5.0", {"start": v(9.12, 1.47) * mm, "end": v(6.63, 1.47) * mm});
            skArc(sketch, "E19.7.5.0", {"start": v(6.63, 5.57) * mm, "mid": v(5.48, 3.52) * mm, "end": v(6.63, 1.47) * mm});
            skLineSegment(sketch, "E19.11.5.0", {"start": v(9.12, 5.57) * mm, "end": v(6.63, 5.57) * mm});
            skArc(sketch, "E19.0.5.1", {"start": v(9.12, 7.97) * mm, "mid": v(10.28, 10.02) * mm, "end": v(9.12, 12.07) * mm});
            skLineSegment(sketch, "E19.4.5.1", {"start": v(9.12, 7.97) * mm, "end": v(6.63, 7.97) * mm});
            skArc(sketch, "E19.7.5.1", {"start": v(6.63, 12.07) * mm, "mid": v(5.48, 10.02) * mm, "end": v(6.63, 7.97) * mm});
            skLineSegment(sketch, "E19.11.5.1", {"start": v(9.12, 12.07) * mm, "end": v(6.63, 12.07) * mm});
            skArc(sketch, "E19.0.5.2", {"start": v(9.12, 14.47) * mm, "mid": v(10.28, 16.52) * mm, "end": v(9.12, 18.57) * mm});
            skLineSegment(sketch, "E19.4.5.2", {"start": v(9.12, 14.47) * mm, "end": v(6.63, 14.47) * mm});
            skArc(sketch, "E19.7.5.2", {"start": v(6.63, 18.57) * mm, "mid": v(5.48, 16.52) * mm, "end": v(6.63, 14.47) * mm});
            skLineSegment(sketch, "E19.11.5.2", {"start": v(9.12, 18.57) * mm, "end": v(6.63, 18.57) * mm});
            skArc(sketch, "E19.0.6.0", {"start": v(15.62, 1.47) * mm, "mid": v(16.78, 3.52) * mm, "end": v(15.62, 5.57) * mm});
            skLineSegment(sketch, "E19.4.6.0", {"start": v(15.62, 1.47) * mm, "end": v(13.13, 1.47) * mm});
            skArc(sketch, "E19.7.6.0", {"start": v(13.13, 5.57) * mm, "mid": v(11.98, 3.52) * mm, "end": v(13.13, 1.47) * mm});
            skLineSegment(sketch, "E19.11.6.0", {"start": v(15.62, 5.57) * mm, "end": v(13.13, 5.57) * mm});
            skArc(sketch, "E19.0.6.1", {"start": v(15.62, 7.97) * mm, "mid": v(16.78, 10.02) * mm, "end": v(15.62, 12.07) * mm});
            skLineSegment(sketch, "E19.4.6.1", {"start": v(15.62, 7.97) * mm, "end": v(13.13, 7.97) * mm});
            skArc(sketch, "E19.7.6.1", {"start": v(13.13, 12.07) * mm, "mid": v(11.98, 10.02) * mm, "end": v(13.13, 7.97) * mm});
            skLineSegment(sketch, "E19.11.6.1", {"start": v(15.62, 12.07) * mm, "end": v(13.13, 12.07) * mm});
            skArc(sketch, "E19.0.6.2", {"start": v(15.62, 14.47) * mm, "mid": v(16.78, 16.52) * mm, "end": v(15.62, 18.57) * mm});
            skLineSegment(sketch, "E19.4.6.2", {"start": v(15.62, 14.47) * mm, "end": v(13.13, 14.47) * mm});
            skArc(sketch, "E19.7.6.2", {"start": v(13.13, 18.57) * mm, "mid": v(11.98, 16.52) * mm, "end": v(13.13, 14.47) * mm});
            skLineSegment(sketch, "E19.11.6.2", {"start": v(15.62, 18.57) * mm, "end": v(13.13, 18.57) * mm});
            skArc(sketch, "E20.0.1.0", {"start": v(-12.87, -0.93) * mm, "mid": v(-14.02, -2.98) * mm, "end": v(-12.87, -5.03) * mm});
            skArc(sketch, "E20.0.1.1", {"start": v(-6.37, -0.93) * mm, "mid": v(-7.52, -2.98) * mm, "end": v(-6.37, -5.03) * mm});
            skLineSegment(sketch, "E20.0.1.2", {"start": v(2.62, -5.03) * mm, "end": v(0.13, -5.03) * mm});
            skLineSegment(sketch, "E20.0.1.3", {"start": v(15.62, -0.93) * mm, "end": v(13.13, -0.93) * mm});
            skArc(sketch, "E20.0.1.4", {"start": v(-19.37, -0.93) * mm, "mid": v(-20.52, -2.98) * mm, "end": v(-19.37, -5.03) * mm});
            skLineSegment(sketch, "E20.0.1.5", {"start": v(9.12, -5.03) * mm, "end": v(6.63, -5.03) * mm});
            skArc(sketch, "E20.0.1.6", {"start": v(15.62, -5.03) * mm, "mid": v(16.78, -2.98) * mm, "end": v(15.62, -0.93) * mm});
            skLineSegment(sketch, "E20.0.1.7", {"start": v(-16.88, -5.03) * mm, "end": v(-19.37, -5.03) * mm});
            skLineSegment(sketch, "E20.0.1.8", {"start": v(-10.38, -0.93) * mm, "end": v(-12.87, -0.93) * mm});
            skArc(sketch, "E20.0.1.9", {"start": v(0.13, -0.93) * mm, "mid": v(-1.02, -2.98) * mm, "end": v(0.13, -5.03) * mm});
            skLineSegment(sketch, "E20.0.1.10", {"start": v(15.62, -5.03) * mm, "end": v(13.13, -5.03) * mm});
            skArc(sketch, "E20.0.1.11", {"start": v(6.63, -0.93) * mm, "mid": v(5.48, -2.98) * mm, "end": v(6.63, -5.03) * mm});
            skLineSegment(sketch, "E20.0.1.12", {"start": v(-23.38, -0.93) * mm, "end": v(-25.87, -0.93) * mm});
            skArc(sketch, "E20.0.1.13", {"start": v(2.62, -5.03) * mm, "mid": v(3.78, -2.98) * mm, "end": v(2.62, -0.93) * mm});
            skArc(sketch, "E20.0.1.14", {"start": v(-10.38, -5.03) * mm, "mid": v(-9.22, -2.98) * mm, "end": v(-10.38, -0.93) * mm});
            skLineSegment(sketch, "E20.0.1.15", {"start": v(-23.38, -5.03) * mm, "end": v(-25.87, -5.03) * mm});
            skArc(sketch, "E20.0.1.16", {"start": v(-3.88, -5.03) * mm, "mid": v(-2.72, -2.98) * mm, "end": v(-3.88, -0.93) * mm});
            skLineSegment(sketch, "E20.0.1.17", {"start": v(-3.88, -0.93) * mm, "end": v(-6.37, -0.93) * mm});
            skLineSegment(sketch, "E20.0.1.18", {"start": v(2.62, -0.93) * mm, "end": v(0.13, -0.93) * mm});
            skLineSegment(sketch, "E20.0.1.19", {"start": v(-10.38, -5.03) * mm, "end": v(-12.87, -5.03) * mm});
            skLineSegment(sketch, "E20.0.1.20", {"start": v(9.12, -0.93) * mm, "end": v(6.63, -0.93) * mm});
            skArc(sketch, "E20.0.1.21", {"start": v(-16.88, -5.03) * mm, "mid": v(-15.72, -2.98) * mm, "end": v(-16.88, -0.93) * mm});
            skLineSegment(sketch, "E20.0.1.22", {"start": v(-3.88, -5.03) * mm, "end": v(-6.37, -5.03) * mm});
            skArc(sketch, "E20.0.1.23", {"start": v(-23.38, -5.03) * mm, "mid": v(-22.22, -2.98) * mm, "end": v(-23.38, -0.93) * mm});
            skArc(sketch, "E20.0.1.24", {"start": v(13.13, -0.93) * mm, "mid": v(11.98, -2.98) * mm, "end": v(13.13, -5.03) * mm});
            skArc(sketch, "E20.0.1.25", {"start": v(9.12, -5.03) * mm, "mid": v(10.28, -2.98) * mm, "end": v(9.12, -0.93) * mm});
            skArc(sketch, "E20.0.1.26", {"start": v(-25.87, -0.93) * mm, "mid": v(-27.02, -2.98) * mm, "end": v(-25.87, -5.03) * mm});
            skLineSegment(sketch, "E20.0.1.27", {"start": v(-16.88, -0.93) * mm, "end": v(-19.37, -0.93) * mm});
            skArc(sketch, "E20.0.2.0", {"start": v(-12.87, -7.43) * mm, "mid": v(-14.02, -9.48) * mm, "end": v(-12.87, -11.53) * mm});
            skArc(sketch, "E20.0.2.1", {"start": v(-6.37, -7.43) * mm, "mid": v(-7.52, -9.48) * mm, "end": v(-6.37, -11.53) * mm});
            skLineSegment(sketch, "E20.0.2.2", {"start": v(2.62, -11.53) * mm, "end": v(0.13, -11.53) * mm});
            skLineSegment(sketch, "E20.0.2.3", {"start": v(15.62, -7.43) * mm, "end": v(13.13, -7.43) * mm});
            skArc(sketch, "E20.0.2.4", {"start": v(-19.37, -7.43) * mm, "mid": v(-20.52, -9.48) * mm, "end": v(-19.37, -11.53) * mm});
            skLineSegment(sketch, "E20.0.2.5", {"start": v(9.12, -11.53) * mm, "end": v(6.63, -11.53) * mm});
            skArc(sketch, "E20.0.2.6", {"start": v(15.62, -11.53) * mm, "mid": v(16.78, -9.48) * mm, "end": v(15.62, -7.43) * mm});
            skLineSegment(sketch, "E20.0.2.7", {"start": v(-16.88, -11.53) * mm, "end": v(-19.37, -11.53) * mm});
            skLineSegment(sketch, "E20.0.2.8", {"start": v(-10.38, -7.43) * mm, "end": v(-12.87, -7.43) * mm});
            skArc(sketch, "E20.0.2.9", {"start": v(0.13, -7.43) * mm, "mid": v(-1.02, -9.48) * mm, "end": v(0.13, -11.53) * mm});
            skLineSegment(sketch, "E20.0.2.10", {"start": v(15.62, -11.53) * mm, "end": v(13.13, -11.53) * mm});
            skArc(sketch, "E20.0.2.11", {"start": v(6.63, -7.43) * mm, "mid": v(5.48, -9.48) * mm, "end": v(6.63, -11.53) * mm});
            skLineSegment(sketch, "E20.0.2.12", {"start": v(-23.38, -7.43) * mm, "end": v(-25.87, -7.43) * mm});
            skArc(sketch, "E20.0.2.13", {"start": v(2.62, -11.53) * mm, "mid": v(3.78, -9.48) * mm, "end": v(2.62, -7.43) * mm});
            skArc(sketch, "E20.0.2.14", {"start": v(-10.38, -11.53) * mm, "mid": v(-9.22, -9.48) * mm, "end": v(-10.38, -7.43) * mm});
            skLineSegment(sketch, "E20.0.2.15", {"start": v(-23.38, -11.53) * mm, "end": v(-25.87, -11.53) * mm});
            skArc(sketch, "E20.0.2.16", {"start": v(-3.88, -11.53) * mm, "mid": v(-2.72, -9.48) * mm, "end": v(-3.88, -7.43) * mm});
            skLineSegment(sketch, "E20.0.2.17", {"start": v(-3.88, -7.43) * mm, "end": v(-6.37, -7.43) * mm});
            skLineSegment(sketch, "E20.0.2.18", {"start": v(2.62, -7.43) * mm, "end": v(0.13, -7.43) * mm});
            skLineSegment(sketch, "E20.0.2.19", {"start": v(-10.38, -11.53) * mm, "end": v(-12.87, -11.53) * mm});
            skLineSegment(sketch, "E20.0.2.20", {"start": v(9.12, -7.43) * mm, "end": v(6.63, -7.43) * mm});
            skArc(sketch, "E20.0.2.21", {"start": v(-16.88, -11.53) * mm, "mid": v(-15.72, -9.48) * mm, "end": v(-16.88, -7.43) * mm});
            skLineSegment(sketch, "E20.0.2.22", {"start": v(-3.88, -11.53) * mm, "end": v(-6.37, -11.53) * mm});
            skArc(sketch, "E20.0.2.23", {"start": v(-23.38, -11.53) * mm, "mid": v(-22.22, -9.48) * mm, "end": v(-23.38, -7.43) * mm});
            skArc(sketch, "E20.0.2.24", {"start": v(13.13, -7.43) * mm, "mid": v(11.98, -9.48) * mm, "end": v(13.13, -11.53) * mm});
            skArc(sketch, "E20.0.2.25", {"start": v(9.12, -11.53) * mm, "mid": v(10.28, -9.48) * mm, "end": v(9.12, -7.43) * mm});
            skArc(sketch, "E20.0.2.26", {"start": v(-25.87, -7.43) * mm, "mid": v(-27.02, -9.48) * mm, "end": v(-25.87, -11.53) * mm});
            skLineSegment(sketch, "E20.0.2.27", {"start": v(-16.88, -7.43) * mm, "end": v(-19.37, -7.43) * mm});
            skArc(sketch, "E20.0.3.0", {"start": v(-12.87, -13.93) * mm, "mid": v(-14.02, -15.98) * mm, "end": v(-12.87, -18.03) * mm});
            skArc(sketch, "E20.0.3.1", {"start": v(-6.37, -13.93) * mm, "mid": v(-7.52, -15.98) * mm, "end": v(-6.37, -18.03) * mm});
            skLineSegment(sketch, "E20.0.3.2", {"start": v(2.62, -18.03) * mm, "end": v(0.13, -18.03) * mm});
            skLineSegment(sketch, "E20.0.3.3", {"start": v(15.62, -13.93) * mm, "end": v(13.13, -13.93) * mm});
            skArc(sketch, "E20.0.3.4", {"start": v(-19.37, -13.93) * mm, "mid": v(-20.52, -15.98) * mm, "end": v(-19.37, -18.03) * mm});
            skLineSegment(sketch, "E20.0.3.5", {"start": v(9.12, -18.03) * mm, "end": v(6.63, -18.03) * mm});
            skArc(sketch, "E20.0.3.6", {"start": v(15.62, -18.03) * mm, "mid": v(16.78, -15.98) * mm, "end": v(15.62, -13.93) * mm});
            skLineSegment(sketch, "E20.0.3.7", {"start": v(-16.88, -18.03) * mm, "end": v(-19.37, -18.03) * mm});
            skLineSegment(sketch, "E20.0.3.8", {"start": v(-10.38, -13.93) * mm, "end": v(-12.87, -13.93) * mm});
            skArc(sketch, "E20.0.3.9", {"start": v(0.13, -13.93) * mm, "mid": v(-1.02, -15.98) * mm, "end": v(0.13, -18.03) * mm});
            skLineSegment(sketch, "E20.0.3.10", {"start": v(15.62, -18.03) * mm, "end": v(13.13, -18.03) * mm});
            skArc(sketch, "E20.0.3.11", {"start": v(6.63, -13.93) * mm, "mid": v(5.48, -15.98) * mm, "end": v(6.63, -18.03) * mm});
            skLineSegment(sketch, "E20.0.3.12", {"start": v(-23.38, -13.93) * mm, "end": v(-25.87, -13.93) * mm});
            skArc(sketch, "E20.0.3.13", {"start": v(2.62, -18.03) * mm, "mid": v(3.78, -15.98) * mm, "end": v(2.62, -13.93) * mm});
            skArc(sketch, "E20.0.3.14", {"start": v(-10.38, -18.03) * mm, "mid": v(-9.22, -15.98) * mm, "end": v(-10.38, -13.93) * mm});
            skLineSegment(sketch, "E20.0.3.15", {"start": v(-23.38, -18.03) * mm, "end": v(-25.87, -18.03) * mm});
            skArc(sketch, "E20.0.3.16", {"start": v(-3.88, -18.03) * mm, "mid": v(-2.72, -15.98) * mm, "end": v(-3.88, -13.93) * mm});
            skLineSegment(sketch, "E20.0.3.17", {"start": v(-3.88, -13.93) * mm, "end": v(-6.37, -13.93) * mm});
            skLineSegment(sketch, "E20.0.3.18", {"start": v(2.62, -13.93) * mm, "end": v(0.13, -13.93) * mm});
            skLineSegment(sketch, "E20.0.3.19", {"start": v(-10.38, -18.03) * mm, "end": v(-12.87, -18.03) * mm});
            skLineSegment(sketch, "E20.0.3.20", {"start": v(9.12, -13.93) * mm, "end": v(6.63, -13.93) * mm});
            skArc(sketch, "E20.0.3.21", {"start": v(-16.88, -18.03) * mm, "mid": v(-15.72, -15.98) * mm, "end": v(-16.88, -13.93) * mm});
            skLineSegment(sketch, "E20.0.3.22", {"start": v(-3.88, -18.03) * mm, "end": v(-6.37, -18.03) * mm});
            skArc(sketch, "E20.0.3.23", {"start": v(-23.38, -18.03) * mm, "mid": v(-22.22, -15.98) * mm, "end": v(-23.38, -13.93) * mm});
            skArc(sketch, "E20.0.3.24", {"start": v(13.13, -13.93) * mm, "mid": v(11.98, -15.98) * mm, "end": v(13.13, -18.03) * mm});
            skArc(sketch, "E20.0.3.25", {"start": v(9.12, -18.03) * mm, "mid": v(10.28, -15.98) * mm, "end": v(9.12, -13.93) * mm});
            skArc(sketch, "E20.0.3.26", {"start": v(-25.87, -13.93) * mm, "mid": v(-27.02, -15.98) * mm, "end": v(-25.87, -18.03) * mm});
            skLineSegment(sketch, "E20.0.3.27", {"start": v(-16.88, -13.93) * mm, "end": v(-19.37, -13.93) * mm});
            skArc(sketch, "E20.0.4.0", {"start": v(-12.87, -20.43) * mm, "mid": v(-14.02, -22.48) * mm, "end": v(-12.87, -24.53) * mm});
            skArc(sketch, "E20.0.4.1", {"start": v(-6.37, -20.43) * mm, "mid": v(-7.52, -22.48) * mm, "end": v(-6.37, -24.53) * mm});
            skLineSegment(sketch, "E20.0.4.2", {"start": v(2.62, -24.53) * mm, "end": v(0.13, -24.53) * mm});
            skLineSegment(sketch, "E20.0.4.3", {"start": v(15.62, -20.43) * mm, "end": v(13.13, -20.43) * mm});
            skArc(sketch, "E20.0.4.4", {"start": v(-19.37, -20.43) * mm, "mid": v(-20.52, -22.48) * mm, "end": v(-19.37, -24.53) * mm});
            skLineSegment(sketch, "E20.0.4.5", {"start": v(9.12, -24.53) * mm, "end": v(6.63, -24.53) * mm});
            skArc(sketch, "E20.0.4.6", {"start": v(15.62, -24.53) * mm, "mid": v(16.78, -22.48) * mm, "end": v(15.62, -20.43) * mm});
            skLineSegment(sketch, "E20.0.4.7", {"start": v(-16.88, -24.53) * mm, "end": v(-19.37, -24.53) * mm});
            skLineSegment(sketch, "E20.0.4.8", {"start": v(-10.38, -20.43) * mm, "end": v(-12.87, -20.43) * mm});
            skArc(sketch, "E20.0.4.9", {"start": v(0.13, -20.43) * mm, "mid": v(-1.02, -22.48) * mm, "end": v(0.13, -24.53) * mm});
            skLineSegment(sketch, "E20.0.4.10", {"start": v(15.62, -24.53) * mm, "end": v(13.13, -24.53) * mm});
            skArc(sketch, "E20.0.4.11", {"start": v(6.63, -20.43) * mm, "mid": v(5.48, -22.48) * mm, "end": v(6.63, -24.53) * mm});
            skLineSegment(sketch, "E20.0.4.12", {"start": v(-23.38, -20.43) * mm, "end": v(-25.87, -20.43) * mm});
            skArc(sketch, "E20.0.4.13", {"start": v(2.62, -24.53) * mm, "mid": v(3.78, -22.48) * mm, "end": v(2.62, -20.43) * mm});
            skArc(sketch, "E20.0.4.14", {"start": v(-10.38, -24.53) * mm, "mid": v(-9.22, -22.48) * mm, "end": v(-10.38, -20.43) * mm});
            skLineSegment(sketch, "E20.0.4.15", {"start": v(-23.38, -24.53) * mm, "end": v(-25.87, -24.53) * mm});
            skArc(sketch, "E20.0.4.16", {"start": v(-3.88, -24.53) * mm, "mid": v(-2.72, -22.48) * mm, "end": v(-3.88, -20.43) * mm});
            skLineSegment(sketch, "E20.0.4.17", {"start": v(-3.88, -20.43) * mm, "end": v(-6.37, -20.43) * mm});
            skLineSegment(sketch, "E20.0.4.18", {"start": v(2.62, -20.43) * mm, "end": v(0.13, -20.43) * mm});
            skLineSegment(sketch, "E20.0.4.19", {"start": v(-10.38, -24.53) * mm, "end": v(-12.87, -24.53) * mm});
            skLineSegment(sketch, "E20.0.4.20", {"start": v(9.12, -20.43) * mm, "end": v(6.63, -20.43) * mm});
            skArc(sketch, "E20.0.4.21", {"start": v(-16.88, -24.53) * mm, "mid": v(-15.72, -22.48) * mm, "end": v(-16.88, -20.43) * mm});
            skLineSegment(sketch, "E20.0.4.22", {"start": v(-3.88, -24.53) * mm, "end": v(-6.37, -24.53) * mm});
            skArc(sketch, "E20.0.4.23", {"start": v(-23.38, -24.53) * mm, "mid": v(-22.22, -22.48) * mm, "end": v(-23.38, -20.43) * mm});
            skArc(sketch, "E20.0.4.24", {"start": v(13.13, -20.43) * mm, "mid": v(11.98, -22.48) * mm, "end": v(13.13, -24.53) * mm});
            skArc(sketch, "E20.0.4.25", {"start": v(9.12, -24.53) * mm, "mid": v(10.28, -22.48) * mm, "end": v(9.12, -20.43) * mm});
            skArc(sketch, "E20.0.4.26", {"start": v(-25.87, -20.43) * mm, "mid": v(-27.02, -22.48) * mm, "end": v(-25.87, -24.53) * mm});
            skLineSegment(sketch, "E20.0.4.27", {"start": v(-16.88, -20.43) * mm, "end": v(-19.37, -20.43) * mm});
            skLineSegment(sketch, "E20.direction1", {"start": v(-25.87, 1.47) * mm, "end": v(-0.9, 1.47) * mm, "construction": true});
            skLineSegment(sketch, "E20.direction2", {"start": v(-25.87, 1.47) * mm, "end": v(-25.87, -5.03) * mm, "construction": true});
            skSolve(sketch);
        }
        {
            var Q0;
            Q0=qSketchRegion(id+"F4",true);
            extrude(context, id + "F5", {"entities" : qUnion([Q0]), "operationType" : NewBodyOperationType.ADD, "oppositeDirection" : true, "depth" : .3 * mm});
        }
    });
